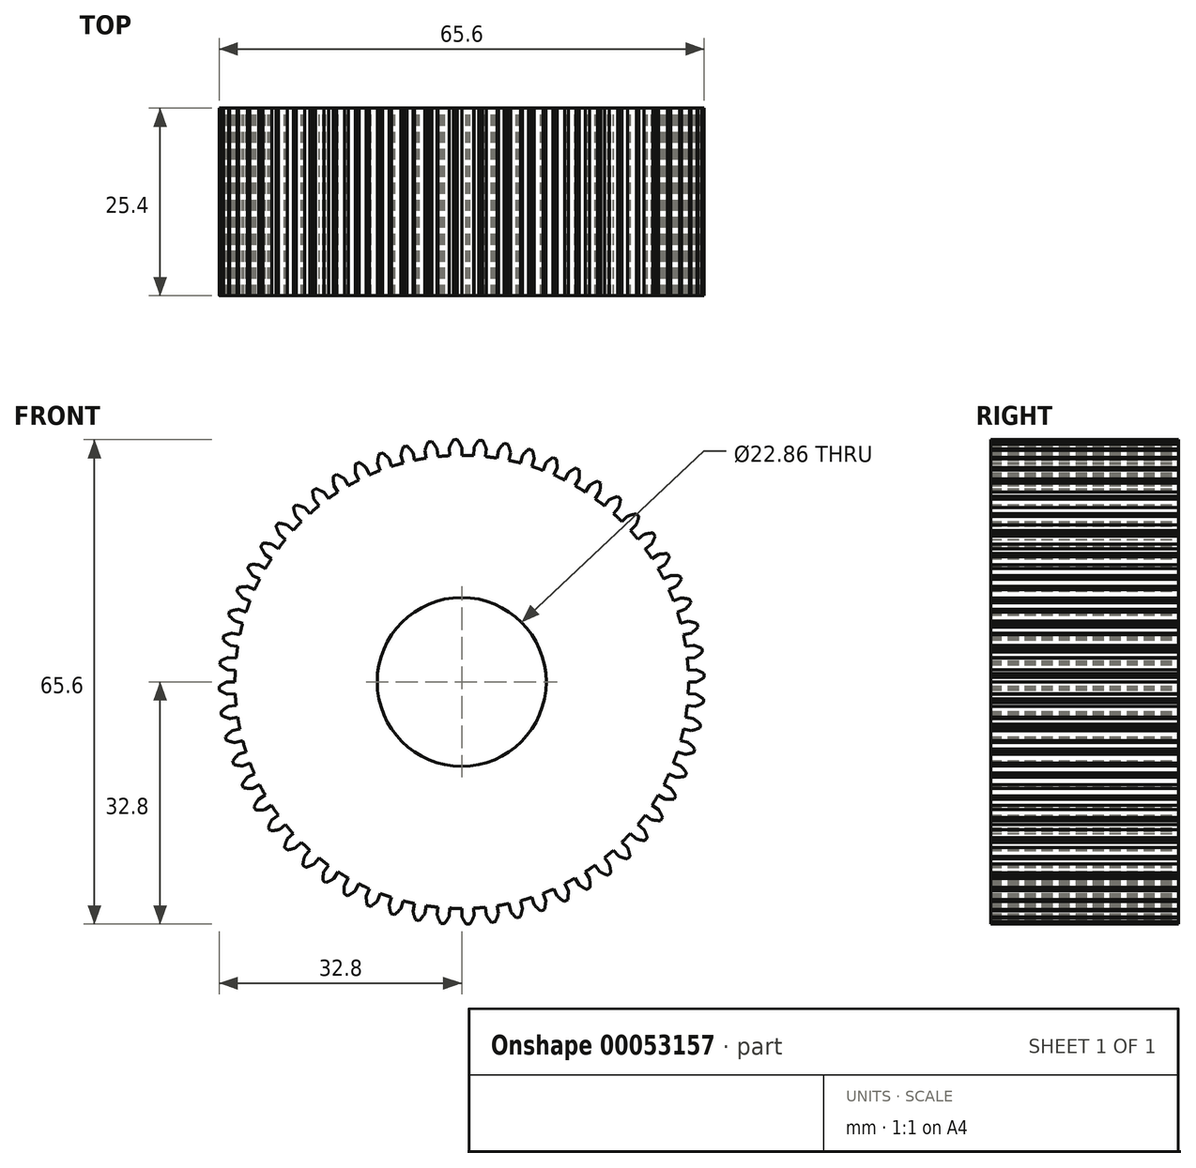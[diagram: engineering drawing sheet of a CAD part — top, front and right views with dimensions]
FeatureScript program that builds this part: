
annotation { "Feature Type Name" : "Feature", "Feature Type Description" : "" }
export const myFeature = defineFeature(function(context is Context, id is Id, definition is map)
    precondition{}
    {
        {
            var Q0;
            Q0=qCreatedBy(makeId("Front.planeOp"),FACE);
            var sketch = newSketch(context, id + "F0", { "sketchPlane" : qUnion([Q0])});
            skArc(sketch, "E0", {"start": v(-7.94, 29.64) * mm, "mid": v(-8.71, 29.42) * mm, "end": v(-9.48, 29.18) * mm});
            skArc(sketch, "E1.trimOffspring", {"start": v(0, 31.75) * mm, "mid": v(-0.28, 32.29) * mm, "end": v(-0.6, 32.8) * mm});
            skLineSegment(sketch, "E2", {"start": v(0, 31.75) * mm, "end": v(0, 30.68) * mm});
            skLineSegment(sketch, "E3", {"start": v(-0.6, 32.8) * mm, "end": v(-0.86, 32.8) * mm});
            skLineSegment(sketch, "E4.MirrorCS", {"start": v(-1.12, 32.79) * mm, "end": v(-0.86, 32.8) * mm});
            skArc(sketch, "E5.MirrorCS", {"start": v(-1.66, 31.7) * mm, "mid": v(-1.4, 32.26) * mm, "end": v(-1.12, 32.79) * mm});
            skLineSegment(sketch, "E6.MirrorCS", {"start": v(-1.66, 31.7) * mm, "end": v(-1.6, 30.64) * mm});
            skLineSegment(sketch, "E7.1.0", {"start": v(-4.97, 31.36) * mm, "end": v(-4.8, 30.3) * mm});
            skArc(sketch, "E7.1.1", {"start": v(-4.97, 31.36) * mm, "mid": v(-4.77, 31.93) * mm, "end": v(-4.54, 32.49) * mm});
            skLineSegment(sketch, "E7.1.2", {"start": v(-4.54, 32.49) * mm, "end": v(-4.28, 32.52) * mm});
            skLineSegment(sketch, "E7.1.3", {"start": v(-4.03, 32.56) * mm, "end": v(-4.28, 32.52) * mm});
            skArc(sketch, "E7.1.4", {"start": v(-3.32, 31.58) * mm, "mid": v(-3.65, 32.08) * mm, "end": v(-4.03, 32.56) * mm});
            skLineSegment(sketch, "E7.1.5", {"start": v(-3.32, 31.58) * mm, "end": v(-3.2, 30.52) * mm});
            skLineSegment(sketch, "E7.2.0", {"start": v(-8.22, 30.67) * mm, "end": v(-7.94, 29.64) * mm});
            skArc(sketch, "E7.2.1", {"start": v(-8.22, 30.67) * mm, "mid": v(-8.08, 31.26) * mm, "end": v(-7.9, 31.84) * mm});
            skLineSegment(sketch, "E7.2.2", {"start": v(-7.9, 31.84) * mm, "end": v(-7.66, 31.9) * mm});
            skLineSegment(sketch, "E7.2.3", {"start": v(-7.4, 31.96) * mm, "end": v(-7.66, 31.9) * mm});
            skArc(sketch, "E7.2.4", {"start": v(-6.6, 31.06) * mm, "mid": v(-6.99, 31.52) * mm, "end": v(-7.4, 31.96) * mm});
            skLineSegment(sketch, "E7.2.5", {"start": v(-6.6, 31.06) * mm, "end": v(-6.38, 30.01) * mm});
            skLineSegment(sketch, "E7.3.0", {"start": v(-11.38, 29.64) * mm, "end": v(-11, 28.65) * mm});
            skArc(sketch, "E7.3.1", {"start": v(-11.38, 29.64) * mm, "mid": v(-11.3, 30.24) * mm, "end": v(-11.2, 30.84) * mm});
            skLineSegment(sketch, "E7.3.2", {"start": v(-11.2, 30.84) * mm, "end": v(-10.95, 30.92) * mm});
            skLineSegment(sketch, "E7.3.3", {"start": v(-10.7, 31) * mm, "end": v(-10.95, 30.92) * mm});
            skArc(sketch, "E7.3.4", {"start": v(-9.81, 30.2) * mm, "mid": v(-10.24, 30.62) * mm, "end": v(-10.7, 31) * mm});
            skLineSegment(sketch, "E7.3.5", {"start": v(-9.81, 30.2) * mm, "end": v(-9.48, 29.18) * mm});
            skLineSegment(sketch, "E7.4.0", {"start": v(-14.41, 28.29) * mm, "end": v(-13.93, 27.34) * mm});
            skArc(sketch, "E7.4.1", {"start": v(-14.41, 28.29) * mm, "mid": v(-14.4, 28.9) * mm, "end": v(-14.35, 29.5) * mm});
            skLineSegment(sketch, "E7.4.2", {"start": v(-14.35, 29.5) * mm, "end": v(-14.12, 29.6) * mm});
            skLineSegment(sketch, "E7.4.3", {"start": v(-13.9, 29.72) * mm, "end": v(-14.12, 29.6) * mm});
            skArc(sketch, "E7.4.4", {"start": v(-12.91, 29) * mm, "mid": v(-13.39, 29.38) * mm, "end": v(-13.9, 29.72) * mm});
            skLineSegment(sketch, "E7.4.5", {"start": v(-12.91, 29) * mm, "end": v(-12.48, 28.03) * mm});
            skLineSegment(sketch, "E7.5.0", {"start": v(-17.3, 26.63) * mm, "end": v(-16.71, 25.73) * mm});
            skArc(sketch, "E7.5.1", {"start": v(-17.3, 26.63) * mm, "mid": v(-17.35, 27.23) * mm, "end": v(-17.36, 27.84) * mm});
            skLineSegment(sketch, "E7.5.2", {"start": v(-17.36, 27.84) * mm, "end": v(-17.14, 27.97) * mm});
            skLineSegment(sketch, "E7.5.3", {"start": v(-16.92, 28.1) * mm, "end": v(-17.14, 27.97) * mm});
            skArc(sketch, "E7.5.4", {"start": v(-15.88, 27.5) * mm, "mid": v(-16.39, 27.82) * mm, "end": v(-16.92, 28.1) * mm});
            skLineSegment(sketch, "E7.5.5", {"start": v(-15.87, 27.5) * mm, "end": v(-15.34, 26.57) * mm});
            skLineSegment(sketch, "E7.6.0", {"start": v(-19.98, 24.67) * mm, "end": v(-19.3, 23.85) * mm});
            skArc(sketch, "E7.6.1", {"start": v(-19.98, 24.67) * mm, "mid": v(-20.1, 25.27) * mm, "end": v(-20.17, 25.87) * mm});
            skLineSegment(sketch, "E7.6.2", {"start": v(-20.17, 25.87) * mm, "end": v(-19.97, 26.03) * mm});
            skLineSegment(sketch, "E7.6.3", {"start": v(-19.77, 26.18) * mm, "end": v(-19.97, 26.03) * mm});
            skArc(sketch, "E7.6.4", {"start": v(-18.66, 25.69) * mm, "mid": v(-19.2, 25.95) * mm, "end": v(-19.77, 26.18) * mm});
            skLineSegment(sketch, "E7.6.5", {"start": v(-18.66, 25.69) * mm, "end": v(-18.04, 24.82) * mm});
            skLineSegment(sketch, "E7.7.0", {"start": v(-22.45, 22.45) * mm, "end": v(-21.7, 21.7) * mm});
            skArc(sketch, "E7.7.1", {"start": v(-22.45, 22.45) * mm, "mid": v(-22.63, 23.03) * mm, "end": v(-22.77, 23.62) * mm});
            skLineSegment(sketch, "E7.7.2", {"start": v(-22.77, 23.62) * mm, "end": v(-22.58, 23.8) * mm});
            skLineSegment(sketch, "E7.7.3", {"start": v(-22.4, 23.97) * mm, "end": v(-22.58, 23.8) * mm});
            skArc(sketch, "E7.7.4", {"start": v(-21.24, 23.6) * mm, "mid": v(-21.81, 23.8) * mm, "end": v(-22.4, 23.97) * mm});
            skLineSegment(sketch, "E7.7.5", {"start": v(-21.24, 23.6) * mm, "end": v(-20.53, 22.8) * mm});
            skLineSegment(sketch, "E7.8.0", {"start": v(-24.67, 19.98) * mm, "end": v(-23.85, 19.3) * mm});
            skArc(sketch, "E7.8.1", {"start": v(-24.67, 19.98) * mm, "mid": v(-24.91, 20.54) * mm, "end": v(-25.11, 21.1) * mm});
            skLineSegment(sketch, "E7.8.2", {"start": v(-25.11, 21.1) * mm, "end": v(-24.95, 21.3) * mm});
            skLineSegment(sketch, "E7.8.3", {"start": v(-24.78, 21.5) * mm, "end": v(-24.95, 21.3) * mm});
            skArc(sketch, "E7.8.4", {"start": v(-23.6, 21.24) * mm, "mid": v(-24.18, 21.4) * mm, "end": v(-24.78, 21.5) * mm});
            skLineSegment(sketch, "E7.8.5", {"start": v(-23.6, 21.24) * mm, "end": v(-22.8, 20.53) * mm});
            skLineSegment(sketch, "E7.9.0", {"start": v(-26.63, 17.3) * mm, "end": v(-25.73, 16.71) * mm});
            skArc(sketch, "E7.9.1", {"start": v(-26.63, 17.3) * mm, "mid": v(-26.92, 17.82) * mm, "end": v(-27.18, 18.37) * mm});
            skLineSegment(sketch, "E7.9.2", {"start": v(-27.18, 18.37) * mm, "end": v(-27.04, 18.58) * mm});
            skLineSegment(sketch, "E7.9.3", {"start": v(-26.89, 18.8) * mm, "end": v(-27.04, 18.58) * mm});
            skArc(sketch, "E7.9.4", {"start": v(-25.69, 18.66) * mm, "mid": v(-26.28, 18.75) * mm, "end": v(-26.89, 18.8) * mm});
            skLineSegment(sketch, "E7.9.5", {"start": v(-25.69, 18.66) * mm, "end": v(-24.82, 18.04) * mm});
            skLineSegment(sketch, "E7.10.0", {"start": v(-28.29, 14.41) * mm, "end": v(-27.34, 13.93) * mm});
            skArc(sketch, "E7.10.1", {"start": v(-28.29, 14.41) * mm, "mid": v(-28.64, 14.9) * mm, "end": v(-28.95, 15.43) * mm});
            skLineSegment(sketch, "E7.10.2", {"start": v(-28.95, 15.43) * mm, "end": v(-28.83, 15.65) * mm});
            skLineSegment(sketch, "E7.10.3", {"start": v(-28.7, 15.88) * mm, "end": v(-28.83, 15.65) * mm});
            skArc(sketch, "E7.10.4", {"start": v(-27.5, 15.88) * mm, "mid": v(-28.1, 15.9) * mm, "end": v(-28.7, 15.88) * mm});
            skLineSegment(sketch, "E7.10.5", {"start": v(-27.5, 15.88) * mm, "end": v(-26.57, 15.34) * mm});
            skLineSegment(sketch, "E7.11.0", {"start": v(-29.64, 11.38) * mm, "end": v(-28.65, 11) * mm});
            skArc(sketch, "E7.11.1", {"start": v(-29.64, 11.38) * mm, "mid": v(-30.04, 11.83) * mm, "end": v(-30.4, 12.32) * mm});
            skLineSegment(sketch, "E7.11.2", {"start": v(-30.4, 12.32) * mm, "end": v(-30.3, 12.55) * mm});
            skLineSegment(sketch, "E7.11.3", {"start": v(-30.2, 12.8) * mm, "end": v(-30.3, 12.55) * mm});
            skArc(sketch, "E7.11.4", {"start": v(-29, 12.91) * mm, "mid": v(-29.6, 12.88) * mm, "end": v(-30.2, 12.8) * mm});
            skLineSegment(sketch, "E7.11.5", {"start": v(-29, 12.91) * mm, "end": v(-28.03, 12.48) * mm});
            skLineSegment(sketch, "E7.12.0", {"start": v(-30.67, 8.22) * mm, "end": v(-29.64, 7.94) * mm});
            skArc(sketch, "E7.12.1", {"start": v(-30.67, 8.22) * mm, "mid": v(-31.11, 8.63) * mm, "end": v(-31.53, 9.07) * mm});
            skLineSegment(sketch, "E7.12.2", {"start": v(-31.53, 9.07) * mm, "end": v(-31.45, 9.32) * mm});
            skLineSegment(sketch, "E7.12.3", {"start": v(-31.38, 9.56) * mm, "end": v(-31.45, 9.32) * mm});
            skArc(sketch, "E7.12.4", {"start": v(-30.2, 9.81) * mm, "mid": v(-30.8, 9.7) * mm, "end": v(-31.38, 9.56) * mm});
            skLineSegment(sketch, "E7.12.5", {"start": v(-30.2, 9.81) * mm, "end": v(-29.18, 9.48) * mm});
            skLineSegment(sketch, "E7.13.0", {"start": v(-31.36, 4.97) * mm, "end": v(-30.3, 4.8) * mm});
            skArc(sketch, "E7.13.1", {"start": v(-31.36, 4.97) * mm, "mid": v(-31.84, 5.33) * mm, "end": v(-32.3, 5.73) * mm});
            skLineSegment(sketch, "E7.13.2", {"start": v(-32.3, 5.73) * mm, "end": v(-32.26, 5.98) * mm});
            skLineSegment(sketch, "E7.13.3", {"start": v(-32.2, 6.23) * mm, "end": v(-32.26, 5.98) * mm});
            skArc(sketch, "E7.13.4", {"start": v(-31.06, 6.6) * mm, "mid": v(-31.64, 6.44) * mm, "end": v(-32.2, 6.23) * mm});
            skLineSegment(sketch, "E7.13.5", {"start": v(-31.06, 6.6) * mm, "end": v(-30.01, 6.38) * mm});
            skLineSegment(sketch, "E7.14.0", {"start": v(-31.7, 1.66) * mm, "end": v(-30.64, 1.6) * mm});
            skArc(sketch, "E7.14.1", {"start": v(-31.7, 1.66) * mm, "mid": v(-32.23, 1.97) * mm, "end": v(-32.72, 2.32) * mm});
            skLineSegment(sketch, "E7.14.2", {"start": v(-32.72, 2.32) * mm, "end": v(-32.7, 2.57) * mm});
            skLineSegment(sketch, "E7.14.3", {"start": v(-32.68, 2.83) * mm, "end": v(-32.7, 2.57) * mm});
            skArc(sketch, "E7.14.4", {"start": v(-31.58, 3.32) * mm, "mid": v(-32.14, 3.1) * mm, "end": v(-32.68, 2.83) * mm});
            skLineSegment(sketch, "E7.14.5", {"start": v(-31.58, 3.32) * mm, "end": v(-30.52, 3.2) * mm});
            skLineSegment(sketch, "E7.15.0", {"start": v(-31.7, -1.66) * mm, "end": v(-30.64, -1.6) * mm});
            skArc(sketch, "E7.15.1", {"start": v(-31.7, -1.66) * mm, "mid": v(-32.26, -1.4) * mm, "end": v(-32.79, -1.12) * mm});
            skLineSegment(sketch, "E7.15.2", {"start": v(-32.79, -1.12) * mm, "end": v(-32.8, -0.86) * mm});
            skLineSegment(sketch, "E7.15.3", {"start": v(-32.8, -0.6) * mm, "end": v(-32.8, -0.86) * mm});
            skArc(sketch, "E7.15.4", {"start": v(-31.75, 0) * mm, "mid": v(-32.29, -0.28) * mm, "end": v(-32.8, -0.6) * mm});
            skLineSegment(sketch, "E7.15.5", {"start": v(-31.75, 0) * mm, "end": v(-30.68, 0) * mm});
            skLineSegment(sketch, "E7.16.0", {"start": v(-31.36, -4.97) * mm, "end": v(-30.3, -4.8) * mm});
            skArc(sketch, "E7.16.1", {"start": v(-31.36, -4.97) * mm, "mid": v(-31.93, -4.77) * mm, "end": v(-32.49, -4.54) * mm});
            skLineSegment(sketch, "E7.16.2", {"start": v(-32.49, -4.54) * mm, "end": v(-32.52, -4.28) * mm});
            skLineSegment(sketch, "E7.16.3", {"start": v(-32.56, -4.03) * mm, "end": v(-32.52, -4.28) * mm});
            skArc(sketch, "E7.16.4", {"start": v(-31.58, -3.32) * mm, "mid": v(-32.08, -3.65) * mm, "end": v(-32.56, -4.03) * mm});
            skLineSegment(sketch, "E7.16.5", {"start": v(-31.58, -3.32) * mm, "end": v(-30.52, -3.2) * mm});
            skLineSegment(sketch, "E7.17.0", {"start": v(-30.67, -8.22) * mm, "end": v(-29.64, -7.94) * mm});
            skArc(sketch, "E7.17.1", {"start": v(-30.67, -8.22) * mm, "mid": v(-31.26, -8.08) * mm, "end": v(-31.84, -7.9) * mm});
            skLineSegment(sketch, "E7.17.2", {"start": v(-31.84, -7.9) * mm, "end": v(-31.9, -7.66) * mm});
            skLineSegment(sketch, "E7.17.3", {"start": v(-31.96, -7.4) * mm, "end": v(-31.9, -7.66) * mm});
            skArc(sketch, "E7.17.4", {"start": v(-31.06, -6.6) * mm, "mid": v(-31.52, -6.99) * mm, "end": v(-31.96, -7.4) * mm});
            skLineSegment(sketch, "E7.17.5", {"start": v(-31.06, -6.6) * mm, "end": v(-30.01, -6.38) * mm});
            skLineSegment(sketch, "E7.18.0", {"start": v(-29.64, -11.38) * mm, "end": v(-28.65, -11) * mm});
            skArc(sketch, "E7.18.1", {"start": v(-29.64, -11.38) * mm, "mid": v(-30.24, -11.3) * mm, "end": v(-30.84, -11.2) * mm});
            skLineSegment(sketch, "E7.18.2", {"start": v(-30.84, -11.2) * mm, "end": v(-30.92, -10.95) * mm});
            skLineSegment(sketch, "E7.18.3", {"start": v(-31, -10.7) * mm, "end": v(-30.92, -10.95) * mm});
            skArc(sketch, "E7.18.4", {"start": v(-30.2, -9.81) * mm, "mid": v(-30.62, -10.24) * mm, "end": v(-31, -10.7) * mm});
            skLineSegment(sketch, "E7.18.5", {"start": v(-30.2, -9.81) * mm, "end": v(-29.18, -9.48) * mm});
            skLineSegment(sketch, "E7.19.0", {"start": v(-28.29, -14.41) * mm, "end": v(-27.34, -13.93) * mm});
            skArc(sketch, "E7.19.1", {"start": v(-28.29, -14.41) * mm, "mid": v(-28.9, -14.4) * mm, "end": v(-29.5, -14.35) * mm});
            skLineSegment(sketch, "E7.19.2", {"start": v(-29.5, -14.35) * mm, "end": v(-29.6, -14.12) * mm});
            skLineSegment(sketch, "E7.19.3", {"start": v(-29.72, -13.9) * mm, "end": v(-29.6, -14.12) * mm});
            skArc(sketch, "E7.19.4", {"start": v(-29, -12.91) * mm, "mid": v(-29.38, -13.39) * mm, "end": v(-29.72, -13.9) * mm});
            skLineSegment(sketch, "E7.19.5", {"start": v(-29, -12.91) * mm, "end": v(-28.03, -12.48) * mm});
            skLineSegment(sketch, "E7.20.0", {"start": v(-26.63, -17.3) * mm, "end": v(-25.73, -16.71) * mm});
            skArc(sketch, "E7.20.1", {"start": v(-26.63, -17.3) * mm, "mid": v(-27.23, -17.35) * mm, "end": v(-27.84, -17.36) * mm});
            skLineSegment(sketch, "E7.20.2", {"start": v(-27.84, -17.36) * mm, "end": v(-27.97, -17.14) * mm});
            skLineSegment(sketch, "E7.20.3", {"start": v(-28.1, -16.92) * mm, "end": v(-27.97, -17.14) * mm});
            skArc(sketch, "E7.20.4", {"start": v(-27.5, -15.87) * mm, "mid": v(-27.82, -16.39) * mm, "end": v(-28.1, -16.92) * mm});
            skLineSegment(sketch, "E7.20.5", {"start": v(-27.5, -15.87) * mm, "end": v(-26.57, -15.34) * mm});
            skLineSegment(sketch, "E7.21.0", {"start": v(-24.67, -19.98) * mm, "end": v(-23.85, -19.3) * mm});
            skArc(sketch, "E7.21.1", {"start": v(-24.67, -19.98) * mm, "mid": v(-25.27, -20.1) * mm, "end": v(-25.87, -20.17) * mm});
            skLineSegment(sketch, "E7.21.2", {"start": v(-25.87, -20.17) * mm, "end": v(-26.03, -19.97) * mm});
            skLineSegment(sketch, "E7.21.3", {"start": v(-26.18, -19.77) * mm, "end": v(-26.03, -19.97) * mm});
            skArc(sketch, "E7.21.4", {"start": v(-25.69, -18.66) * mm, "mid": v(-25.95, -19.2) * mm, "end": v(-26.18, -19.77) * mm});
            skLineSegment(sketch, "E7.21.5", {"start": v(-25.69, -18.66) * mm, "end": v(-24.82, -18.04) * mm});
            skLineSegment(sketch, "E7.22.0", {"start": v(-22.45, -22.45) * mm, "end": v(-21.7, -21.7) * mm});
            skArc(sketch, "E7.22.1", {"start": v(-22.45, -22.45) * mm, "mid": v(-23.03, -22.63) * mm, "end": v(-23.62, -22.77) * mm});
            skLineSegment(sketch, "E7.22.2", {"start": v(-23.62, -22.77) * mm, "end": v(-23.8, -22.58) * mm});
            skLineSegment(sketch, "E7.22.3", {"start": v(-23.97, -22.4) * mm, "end": v(-23.8, -22.58) * mm});
            skArc(sketch, "E7.22.4", {"start": v(-23.6, -21.24) * mm, "mid": v(-23.8, -21.81) * mm, "end": v(-23.97, -22.4) * mm});
            skLineSegment(sketch, "E7.22.5", {"start": v(-23.6, -21.24) * mm, "end": v(-22.8, -20.53) * mm});
            skLineSegment(sketch, "E7.23.0", {"start": v(-19.98, -24.67) * mm, "end": v(-19.3, -23.85) * mm});
            skArc(sketch, "E7.23.1", {"start": v(-19.98, -24.67) * mm, "mid": v(-20.54, -24.91) * mm, "end": v(-21.1, -25.11) * mm});
            skLineSegment(sketch, "E7.23.2", {"start": v(-21.1, -25.11) * mm, "end": v(-21.3, -24.95) * mm});
            skLineSegment(sketch, "E7.23.3", {"start": v(-21.5, -24.78) * mm, "end": v(-21.3, -24.95) * mm});
            skArc(sketch, "E7.23.4", {"start": v(-21.24, -23.6) * mm, "mid": v(-21.4, -24.18) * mm, "end": v(-21.5, -24.78) * mm});
            skLineSegment(sketch, "E7.23.5", {"start": v(-21.24, -23.6) * mm, "end": v(-20.53, -22.8) * mm});
            skLineSegment(sketch, "E7.24.0", {"start": v(-17.3, -26.63) * mm, "end": v(-16.71, -25.73) * mm});
            skArc(sketch, "E7.24.1", {"start": v(-17.3, -26.63) * mm, "mid": v(-17.82, -26.92) * mm, "end": v(-18.37, -27.18) * mm});
            skLineSegment(sketch, "E7.24.2", {"start": v(-18.37, -27.18) * mm, "end": v(-18.58, -27.04) * mm});
            skLineSegment(sketch, "E7.24.3", {"start": v(-18.8, -26.89) * mm, "end": v(-18.58, -27.04) * mm});
            skArc(sketch, "E7.24.4", {"start": v(-18.66, -25.69) * mm, "mid": v(-18.75, -26.28) * mm, "end": v(-18.8, -26.89) * mm});
            skLineSegment(sketch, "E7.24.5", {"start": v(-18.66, -25.69) * mm, "end": v(-18.04, -24.82) * mm});
            skLineSegment(sketch, "E7.25.0", {"start": v(-14.41, -28.29) * mm, "end": v(-13.93, -27.34) * mm});
            skArc(sketch, "E7.25.1", {"start": v(-14.41, -28.29) * mm, "mid": v(-14.9, -28.64) * mm, "end": v(-15.43, -28.95) * mm});
            skLineSegment(sketch, "E7.25.2", {"start": v(-15.43, -28.95) * mm, "end": v(-15.65, -28.83) * mm});
            skLineSegment(sketch, "E7.25.3", {"start": v(-15.88, -28.7) * mm, "end": v(-15.65, -28.83) * mm});
            skArc(sketch, "E7.25.4", {"start": v(-15.87, -27.5) * mm, "mid": v(-15.9, -28.1) * mm, "end": v(-15.88, -28.7) * mm});
            skLineSegment(sketch, "E7.25.5", {"start": v(-15.87, -27.5) * mm, "end": v(-15.34, -26.57) * mm});
            skLineSegment(sketch, "E7.26.0", {"start": v(-11.38, -29.64) * mm, "end": v(-11, -28.65) * mm});
            skArc(sketch, "E7.26.1", {"start": v(-11.38, -29.64) * mm, "mid": v(-11.83, -30.04) * mm, "end": v(-12.32, -30.4) * mm});
            skLineSegment(sketch, "E7.26.2", {"start": v(-12.32, -30.4) * mm, "end": v(-12.55, -30.3) * mm});
            skLineSegment(sketch, "E7.26.3", {"start": v(-12.8, -30.2) * mm, "end": v(-12.55, -30.3) * mm});
            skArc(sketch, "E7.26.4", {"start": v(-12.91, -29) * mm, "mid": v(-12.88, -29.6) * mm, "end": v(-12.8, -30.2) * mm});
            skLineSegment(sketch, "E7.26.5", {"start": v(-12.91, -29) * mm, "end": v(-12.48, -28.03) * mm});
            skLineSegment(sketch, "E7.27.0", {"start": v(-8.22, -30.67) * mm, "end": v(-7.94, -29.64) * mm});
            skArc(sketch, "E7.27.1", {"start": v(-8.22, -30.67) * mm, "mid": v(-8.63, -31.11) * mm, "end": v(-9.07, -31.53) * mm});
            skLineSegment(sketch, "E7.27.2", {"start": v(-9.07, -31.53) * mm, "end": v(-9.32, -31.45) * mm});
            skLineSegment(sketch, "E7.27.3", {"start": v(-9.56, -31.38) * mm, "end": v(-9.32, -31.45) * mm});
            skArc(sketch, "E7.27.4", {"start": v(-9.81, -30.2) * mm, "mid": v(-9.7, -30.8) * mm, "end": v(-9.56, -31.38) * mm});
            skLineSegment(sketch, "E7.27.5", {"start": v(-9.81, -30.2) * mm, "end": v(-9.48, -29.18) * mm});
            skLineSegment(sketch, "E7.28.0", {"start": v(-4.97, -31.36) * mm, "end": v(-4.8, -30.3) * mm});
            skArc(sketch, "E7.28.1", {"start": v(-4.97, -31.36) * mm, "mid": v(-5.33, -31.84) * mm, "end": v(-5.73, -32.3) * mm});
            skLineSegment(sketch, "E7.28.2", {"start": v(-5.73, -32.3) * mm, "end": v(-5.98, -32.26) * mm});
            skLineSegment(sketch, "E7.28.3", {"start": v(-6.23, -32.2) * mm, "end": v(-5.98, -32.26) * mm});
            skArc(sketch, "E7.28.4", {"start": v(-6.6, -31.06) * mm, "mid": v(-6.44, -31.64) * mm, "end": v(-6.23, -32.2) * mm});
            skLineSegment(sketch, "E7.28.5", {"start": v(-6.6, -31.06) * mm, "end": v(-6.38, -30.01) * mm});
            skLineSegment(sketch, "E7.29.0", {"start": v(-1.66, -31.7) * mm, "end": v(-1.6, -30.64) * mm});
            skArc(sketch, "E7.29.1", {"start": v(-1.66, -31.7) * mm, "mid": v(-1.97, -32.23) * mm, "end": v(-2.32, -32.72) * mm});
            skLineSegment(sketch, "E7.29.2", {"start": v(-2.32, -32.72) * mm, "end": v(-2.57, -32.7) * mm});
            skLineSegment(sketch, "E7.29.3", {"start": v(-2.83, -32.68) * mm, "end": v(-2.57, -32.7) * mm});
            skArc(sketch, "E7.29.4", {"start": v(-3.32, -31.58) * mm, "mid": v(-3.1, -32.14) * mm, "end": v(-2.83, -32.68) * mm});
            skLineSegment(sketch, "E7.29.5", {"start": v(-3.32, -31.58) * mm, "end": v(-3.2, -30.52) * mm});
            skLineSegment(sketch, "E7.30.0", {"start": v(1.66, -31.7) * mm, "end": v(1.6, -30.64) * mm});
            skArc(sketch, "E7.30.1", {"start": v(1.66, -31.7) * mm, "mid": v(1.4, -32.26) * mm, "end": v(1.12, -32.79) * mm});
            skLineSegment(sketch, "E7.30.2", {"start": v(1.12, -32.79) * mm, "end": v(0.86, -32.8) * mm});
            skLineSegment(sketch, "E7.30.3", {"start": v(0.6, -32.8) * mm, "end": v(0.86, -32.8) * mm});
            skArc(sketch, "E7.30.4", {"start": v(0, -31.75) * mm, "mid": v(0.28, -32.29) * mm, "end": v(0.6, -32.8) * mm});
            skLineSegment(sketch, "E7.30.5", {"start": v(0, -31.75) * mm, "end": v(0, -30.68) * mm});
            skLineSegment(sketch, "E7.31.0", {"start": v(4.97, -31.36) * mm, "end": v(4.8, -30.3) * mm});
            skArc(sketch, "E7.31.1", {"start": v(4.97, -31.36) * mm, "mid": v(4.77, -31.93) * mm, "end": v(4.54, -32.49) * mm});
            skLineSegment(sketch, "E7.31.2", {"start": v(4.54, -32.49) * mm, "end": v(4.28, -32.52) * mm});
            skLineSegment(sketch, "E7.31.3", {"start": v(4.03, -32.56) * mm, "end": v(4.28, -32.52) * mm});
            skArc(sketch, "E7.31.4", {"start": v(3.32, -31.58) * mm, "mid": v(3.65, -32.08) * mm, "end": v(4.03, -32.56) * mm});
            skLineSegment(sketch, "E7.31.5", {"start": v(3.32, -31.58) * mm, "end": v(3.2, -30.52) * mm});
            skLineSegment(sketch, "E7.32.0", {"start": v(8.22, -30.67) * mm, "end": v(7.94, -29.64) * mm});
            skArc(sketch, "E7.32.1", {"start": v(8.22, -30.67) * mm, "mid": v(8.08, -31.26) * mm, "end": v(7.9, -31.84) * mm});
            skLineSegment(sketch, "E7.32.2", {"start": v(7.9, -31.84) * mm, "end": v(7.66, -31.9) * mm});
            skLineSegment(sketch, "E7.32.3", {"start": v(7.4, -31.96) * mm, "end": v(7.66, -31.9) * mm});
            skArc(sketch, "E7.32.4", {"start": v(6.6, -31.06) * mm, "mid": v(6.99, -31.52) * mm, "end": v(7.4, -31.96) * mm});
            skLineSegment(sketch, "E7.32.5", {"start": v(6.6, -31.06) * mm, "end": v(6.38, -30.01) * mm});
            skLineSegment(sketch, "E7.33.0", {"start": v(11.38, -29.64) * mm, "end": v(11, -28.65) * mm});
            skArc(sketch, "E7.33.1", {"start": v(11.38, -29.64) * mm, "mid": v(11.3, -30.24) * mm, "end": v(11.2, -30.84) * mm});
            skLineSegment(sketch, "E7.33.2", {"start": v(11.2, -30.84) * mm, "end": v(10.95, -30.92) * mm});
            skLineSegment(sketch, "E7.33.3", {"start": v(10.7, -31) * mm, "end": v(10.95, -30.92) * mm});
            skArc(sketch, "E7.33.4", {"start": v(9.81, -30.2) * mm, "mid": v(10.24, -30.62) * mm, "end": v(10.7, -31) * mm});
            skLineSegment(sketch, "E7.33.5", {"start": v(9.81, -30.2) * mm, "end": v(9.48, -29.18) * mm});
            skLineSegment(sketch, "E7.34.0", {"start": v(14.41, -28.29) * mm, "end": v(13.93, -27.34) * mm});
            skArc(sketch, "E7.34.1", {"start": v(14.41, -28.29) * mm, "mid": v(14.4, -28.9) * mm, "end": v(14.35, -29.5) * mm});
            skLineSegment(sketch, "E7.34.2", {"start": v(14.35, -29.5) * mm, "end": v(14.12, -29.6) * mm});
            skLineSegment(sketch, "E7.34.3", {"start": v(13.9, -29.72) * mm, "end": v(14.12, -29.6) * mm});
            skArc(sketch, "E7.34.4", {"start": v(12.91, -29) * mm, "mid": v(13.39, -29.38) * mm, "end": v(13.9, -29.72) * mm});
            skLineSegment(sketch, "E7.34.5", {"start": v(12.91, -29) * mm, "end": v(12.48, -28.03) * mm});
            skLineSegment(sketch, "E7.35.0", {"start": v(17.3, -26.63) * mm, "end": v(16.71, -25.73) * mm});
            skArc(sketch, "E7.35.1", {"start": v(17.3, -26.63) * mm, "mid": v(17.35, -27.23) * mm, "end": v(17.36, -27.84) * mm});
            skLineSegment(sketch, "E7.35.2", {"start": v(17.36, -27.84) * mm, "end": v(17.14, -27.97) * mm});
            skLineSegment(sketch, "E7.35.3", {"start": v(16.92, -28.1) * mm, "end": v(17.14, -27.97) * mm});
            skArc(sketch, "E7.35.4", {"start": v(15.87, -27.5) * mm, "mid": v(16.39, -27.82) * mm, "end": v(16.92, -28.1) * mm});
            skLineSegment(sketch, "E7.35.5", {"start": v(15.87, -27.5) * mm, "end": v(15.34, -26.57) * mm});
            skLineSegment(sketch, "E7.36.0", {"start": v(19.98, -24.67) * mm, "end": v(19.3, -23.85) * mm});
            skArc(sketch, "E7.36.1", {"start": v(19.98, -24.67) * mm, "mid": v(20.1, -25.27) * mm, "end": v(20.17, -25.87) * mm});
            skLineSegment(sketch, "E7.36.2", {"start": v(20.17, -25.87) * mm, "end": v(19.97, -26.03) * mm});
            skLineSegment(sketch, "E7.36.3", {"start": v(19.77, -26.18) * mm, "end": v(19.97, -26.03) * mm});
            skArc(sketch, "E7.36.4", {"start": v(18.66, -25.69) * mm, "mid": v(19.2, -25.95) * mm, "end": v(19.77, -26.18) * mm});
            skLineSegment(sketch, "E7.36.5", {"start": v(18.66, -25.69) * mm, "end": v(18.04, -24.82) * mm});
            skLineSegment(sketch, "E7.37.0", {"start": v(22.45, -22.45) * mm, "end": v(21.7, -21.7) * mm});
            skArc(sketch, "E7.37.1", {"start": v(22.45, -22.45) * mm, "mid": v(22.63, -23.03) * mm, "end": v(22.77, -23.62) * mm});
            skLineSegment(sketch, "E7.37.2", {"start": v(22.77, -23.62) * mm, "end": v(22.58, -23.8) * mm});
            skLineSegment(sketch, "E7.37.3", {"start": v(22.4, -23.97) * mm, "end": v(22.58, -23.8) * mm});
            skArc(sketch, "E7.37.4", {"start": v(21.24, -23.6) * mm, "mid": v(21.81, -23.8) * mm, "end": v(22.4, -23.97) * mm});
            skLineSegment(sketch, "E7.37.5", {"start": v(21.24, -23.6) * mm, "end": v(20.53, -22.8) * mm});
            skLineSegment(sketch, "E7.38.0", {"start": v(24.67, -19.98) * mm, "end": v(23.85, -19.3) * mm});
            skArc(sketch, "E7.38.1", {"start": v(24.67, -19.98) * mm, "mid": v(24.91, -20.54) * mm, "end": v(25.11, -21.1) * mm});
            skLineSegment(sketch, "E7.38.2", {"start": v(25.11, -21.1) * mm, "end": v(24.95, -21.3) * mm});
            skLineSegment(sketch, "E7.38.3", {"start": v(24.78, -21.5) * mm, "end": v(24.95, -21.3) * mm});
            skArc(sketch, "E7.38.4", {"start": v(23.6, -21.24) * mm, "mid": v(24.18, -21.4) * mm, "end": v(24.78, -21.5) * mm});
            skLineSegment(sketch, "E7.38.5", {"start": v(23.6, -21.24) * mm, "end": v(22.8, -20.53) * mm});
            skLineSegment(sketch, "E7.39.0", {"start": v(26.63, -17.3) * mm, "end": v(25.73, -16.71) * mm});
            skArc(sketch, "E7.39.1", {"start": v(26.63, -17.3) * mm, "mid": v(26.92, -17.82) * mm, "end": v(27.18, -18.37) * mm});
            skLineSegment(sketch, "E7.39.2", {"start": v(27.18, -18.37) * mm, "end": v(27.04, -18.58) * mm});
            skLineSegment(sketch, "E7.39.3", {"start": v(26.89, -18.8) * mm, "end": v(27.04, -18.58) * mm});
            skArc(sketch, "E7.39.4", {"start": v(25.69, -18.66) * mm, "mid": v(26.28, -18.75) * mm, "end": v(26.89, -18.8) * mm});
            skLineSegment(sketch, "E7.39.5", {"start": v(25.69, -18.66) * mm, "end": v(24.82, -18.04) * mm});
            skLineSegment(sketch, "E7.40.0", {"start": v(28.29, -14.41) * mm, "end": v(27.34, -13.93) * mm});
            skArc(sketch, "E7.40.1", {"start": v(28.29, -14.41) * mm, "mid": v(28.64, -14.9) * mm, "end": v(28.95, -15.43) * mm});
            skLineSegment(sketch, "E7.40.2", {"start": v(28.95, -15.43) * mm, "end": v(28.83, -15.65) * mm});
            skLineSegment(sketch, "E7.40.3", {"start": v(28.7, -15.88) * mm, "end": v(28.83, -15.65) * mm});
            skArc(sketch, "E7.40.4", {"start": v(27.5, -15.88) * mm, "mid": v(28.1, -15.9) * mm, "end": v(28.7, -15.88) * mm});
            skLineSegment(sketch, "E7.40.5", {"start": v(27.5, -15.88) * mm, "end": v(26.57, -15.34) * mm});
            skLineSegment(sketch, "E7.41.0", {"start": v(29.64, -11.38) * mm, "end": v(28.65, -11) * mm});
            skArc(sketch, "E7.41.1", {"start": v(29.64, -11.38) * mm, "mid": v(30.04, -11.83) * mm, "end": v(30.4, -12.32) * mm});
            skLineSegment(sketch, "E7.41.2", {"start": v(30.4, -12.32) * mm, "end": v(30.3, -12.55) * mm});
            skLineSegment(sketch, "E7.41.3", {"start": v(30.2, -12.8) * mm, "end": v(30.3, -12.55) * mm});
            skArc(sketch, "E7.41.4", {"start": v(29, -12.91) * mm, "mid": v(29.6, -12.88) * mm, "end": v(30.2, -12.8) * mm});
            skLineSegment(sketch, "E7.41.5", {"start": v(29, -12.91) * mm, "end": v(28.03, -12.48) * mm});
            skLineSegment(sketch, "E7.42.0", {"start": v(30.67, -8.22) * mm, "end": v(29.64, -7.94) * mm});
            skArc(sketch, "E7.42.1", {"start": v(30.67, -8.22) * mm, "mid": v(31.11, -8.63) * mm, "end": v(31.53, -9.07) * mm});
            skLineSegment(sketch, "E7.42.2", {"start": v(31.53, -9.07) * mm, "end": v(31.45, -9.32) * mm});
            skLineSegment(sketch, "E7.42.3", {"start": v(31.38, -9.56) * mm, "end": v(31.45, -9.32) * mm});
            skArc(sketch, "E7.42.4", {"start": v(30.2, -9.81) * mm, "mid": v(30.8, -9.7) * mm, "end": v(31.38, -9.56) * mm});
            skLineSegment(sketch, "E7.42.5", {"start": v(30.2, -9.81) * mm, "end": v(29.18, -9.48) * mm});
            skLineSegment(sketch, "E7.43.0", {"start": v(31.36, -4.97) * mm, "end": v(30.3, -4.8) * mm});
            skArc(sketch, "E7.43.1", {"start": v(31.36, -4.97) * mm, "mid": v(31.84, -5.33) * mm, "end": v(32.3, -5.73) * mm});
            skLineSegment(sketch, "E7.43.2", {"start": v(32.3, -5.73) * mm, "end": v(32.26, -5.98) * mm});
            skLineSegment(sketch, "E7.43.3", {"start": v(32.2, -6.23) * mm, "end": v(32.26, -5.98) * mm});
            skArc(sketch, "E7.43.4", {"start": v(31.06, -6.6) * mm, "mid": v(31.64, -6.44) * mm, "end": v(32.2, -6.23) * mm});
            skLineSegment(sketch, "E7.43.5", {"start": v(31.06, -6.6) * mm, "end": v(30.01, -6.38) * mm});
            skLineSegment(sketch, "E7.44.0", {"start": v(31.7, -1.66) * mm, "end": v(30.64, -1.6) * mm});
            skArc(sketch, "E7.44.1", {"start": v(31.7, -1.66) * mm, "mid": v(32.23, -1.97) * mm, "end": v(32.72, -2.32) * mm});
            skLineSegment(sketch, "E7.44.2", {"start": v(32.72, -2.32) * mm, "end": v(32.7, -2.57) * mm});
            skLineSegment(sketch, "E7.44.3", {"start": v(32.68, -2.83) * mm, "end": v(32.7, -2.57) * mm});
            skArc(sketch, "E7.44.4", {"start": v(31.58, -3.32) * mm, "mid": v(32.14, -3.1) * mm, "end": v(32.68, -2.83) * mm});
            skLineSegment(sketch, "E7.44.5", {"start": v(31.58, -3.32) * mm, "end": v(30.52, -3.2) * mm});
            skLineSegment(sketch, "E7.45.0", {"start": v(31.7, 1.66) * mm, "end": v(30.64, 1.6) * mm});
            skArc(sketch, "E7.45.1", {"start": v(31.7, 1.66) * mm, "mid": v(32.26, 1.4) * mm, "end": v(32.79, 1.12) * mm});
            skLineSegment(sketch, "E7.45.2", {"start": v(32.79, 1.12) * mm, "end": v(32.8, 0.86) * mm});
            skLineSegment(sketch, "E7.45.3", {"start": v(32.8, 0.6) * mm, "end": v(32.8, 0.86) * mm});
            skArc(sketch, "E7.45.4", {"start": v(31.75, 0) * mm, "mid": v(32.29, 0.28) * mm, "end": v(32.8, 0.6) * mm});
            skLineSegment(sketch, "E7.45.5", {"start": v(31.75, 0) * mm, "end": v(30.68, 0) * mm});
            skLineSegment(sketch, "E7.46.0", {"start": v(31.36, 4.97) * mm, "end": v(30.3, 4.8) * mm});
            skArc(sketch, "E7.46.1", {"start": v(31.36, 4.97) * mm, "mid": v(31.93, 4.77) * mm, "end": v(32.49, 4.54) * mm});
            skLineSegment(sketch, "E7.46.2", {"start": v(32.49, 4.54) * mm, "end": v(32.52, 4.28) * mm});
            skLineSegment(sketch, "E7.46.3", {"start": v(32.56, 4.03) * mm, "end": v(32.52, 4.28) * mm});
            skArc(sketch, "E7.46.4", {"start": v(31.58, 3.32) * mm, "mid": v(32.08, 3.65) * mm, "end": v(32.56, 4.03) * mm});
            skLineSegment(sketch, "E7.46.5", {"start": v(31.58, 3.32) * mm, "end": v(30.52, 3.2) * mm});
            skLineSegment(sketch, "E7.47.0", {"start": v(30.67, 8.22) * mm, "end": v(29.64, 7.94) * mm});
            skArc(sketch, "E7.47.1", {"start": v(30.67, 8.22) * mm, "mid": v(31.26, 8.08) * mm, "end": v(31.84, 7.9) * mm});
            skLineSegment(sketch, "E7.47.2", {"start": v(31.84, 7.9) * mm, "end": v(31.9, 7.66) * mm});
            skLineSegment(sketch, "E7.47.3", {"start": v(31.96, 7.4) * mm, "end": v(31.9, 7.66) * mm});
            skArc(sketch, "E7.47.4", {"start": v(31.06, 6.6) * mm, "mid": v(31.52, 6.99) * mm, "end": v(31.96, 7.4) * mm});
            skLineSegment(sketch, "E7.47.5", {"start": v(31.06, 6.6) * mm, "end": v(30.01, 6.38) * mm});
            skLineSegment(sketch, "E7.48.0", {"start": v(29.64, 11.38) * mm, "end": v(28.65, 11) * mm});
            skArc(sketch, "E7.48.1", {"start": v(29.64, 11.38) * mm, "mid": v(30.24, 11.3) * mm, "end": v(30.84, 11.2) * mm});
            skLineSegment(sketch, "E7.48.2", {"start": v(30.84, 11.2) * mm, "end": v(30.92, 10.95) * mm});
            skLineSegment(sketch, "E7.48.3", {"start": v(31, 10.7) * mm, "end": v(30.92, 10.95) * mm});
            skArc(sketch, "E7.48.4", {"start": v(30.2, 9.81) * mm, "mid": v(30.62, 10.24) * mm, "end": v(31, 10.7) * mm});
            skLineSegment(sketch, "E7.48.5", {"start": v(30.2, 9.81) * mm, "end": v(29.18, 9.48) * mm});
            skLineSegment(sketch, "E7.49.0", {"start": v(28.29, 14.41) * mm, "end": v(27.34, 13.93) * mm});
            skArc(sketch, "E7.49.1", {"start": v(28.29, 14.41) * mm, "mid": v(28.9, 14.4) * mm, "end": v(29.5, 14.35) * mm});
            skLineSegment(sketch, "E7.49.2", {"start": v(29.5, 14.35) * mm, "end": v(29.6, 14.12) * mm});
            skLineSegment(sketch, "E7.49.3", {"start": v(29.72, 13.9) * mm, "end": v(29.6, 14.12) * mm});
            skArc(sketch, "E7.49.4", {"start": v(29, 12.91) * mm, "mid": v(29.38, 13.39) * mm, "end": v(29.72, 13.9) * mm});
            skLineSegment(sketch, "E7.49.5", {"start": v(29, 12.91) * mm, "end": v(28.03, 12.48) * mm});
            skLineSegment(sketch, "E7.50.0", {"start": v(26.63, 17.3) * mm, "end": v(25.73, 16.71) * mm});
            skArc(sketch, "E7.50.1", {"start": v(26.63, 17.3) * mm, "mid": v(27.23, 17.35) * mm, "end": v(27.84, 17.36) * mm});
            skLineSegment(sketch, "E7.50.2", {"start": v(27.84, 17.36) * mm, "end": v(27.97, 17.14) * mm});
            skLineSegment(sketch, "E7.50.3", {"start": v(28.1, 16.92) * mm, "end": v(27.97, 17.14) * mm});
            skArc(sketch, "E7.50.4", {"start": v(27.5, 15.88) * mm, "mid": v(27.82, 16.39) * mm, "end": v(28.1, 16.92) * mm});
            skLineSegment(sketch, "E7.50.5", {"start": v(27.5, 15.88) * mm, "end": v(26.57, 15.34) * mm});
            skLineSegment(sketch, "E7.51.0", {"start": v(24.67, 19.98) * mm, "end": v(23.85, 19.3) * mm});
            skArc(sketch, "E7.51.1", {"start": v(24.67, 19.98) * mm, "mid": v(25.27, 20.1) * mm, "end": v(25.87, 20.17) * mm});
            skLineSegment(sketch, "E7.51.2", {"start": v(25.87, 20.17) * mm, "end": v(26.03, 19.97) * mm});
            skLineSegment(sketch, "E7.51.3", {"start": v(26.18, 19.77) * mm, "end": v(26.03, 19.97) * mm});
            skArc(sketch, "E7.51.4", {"start": v(25.69, 18.66) * mm, "mid": v(25.95, 19.2) * mm, "end": v(26.18, 19.77) * mm});
            skLineSegment(sketch, "E7.51.5", {"start": v(25.69, 18.66) * mm, "end": v(24.82, 18.04) * mm});
            skLineSegment(sketch, "E7.52.0", {"start": v(22.45, 22.45) * mm, "end": v(21.7, 21.7) * mm});
            skArc(sketch, "E7.52.1", {"start": v(22.45, 22.45) * mm, "mid": v(23.03, 22.63) * mm, "end": v(23.62, 22.77) * mm});
            skLineSegment(sketch, "E7.52.2", {"start": v(23.62, 22.77) * mm, "end": v(23.8, 22.58) * mm});
            skLineSegment(sketch, "E7.52.3", {"start": v(23.97, 22.4) * mm, "end": v(23.8, 22.58) * mm});
            skArc(sketch, "E7.52.4", {"start": v(23.6, 21.24) * mm, "mid": v(23.8, 21.81) * mm, "end": v(23.97, 22.4) * mm});
            skLineSegment(sketch, "E7.52.5", {"start": v(23.6, 21.24) * mm, "end": v(22.8, 20.53) * mm});
            skLineSegment(sketch, "E7.53.0", {"start": v(19.98, 24.67) * mm, "end": v(19.3, 23.85) * mm});
            skArc(sketch, "E7.53.1", {"start": v(19.98, 24.67) * mm, "mid": v(20.54, 24.91) * mm, "end": v(21.1, 25.11) * mm});
            skLineSegment(sketch, "E7.53.2", {"start": v(21.1, 25.11) * mm, "end": v(21.3, 24.95) * mm});
            skLineSegment(sketch, "E7.53.3", {"start": v(21.5, 24.78) * mm, "end": v(21.3, 24.95) * mm});
            skArc(sketch, "E7.53.4", {"start": v(21.24, 23.6) * mm, "mid": v(21.4, 24.18) * mm, "end": v(21.5, 24.78) * mm});
            skLineSegment(sketch, "E7.53.5", {"start": v(21.24, 23.6) * mm, "end": v(20.53, 22.8) * mm});
            skLineSegment(sketch, "E7.54.0", {"start": v(17.3, 26.63) * mm, "end": v(16.71, 25.73) * mm});
            skArc(sketch, "E7.54.1", {"start": v(17.3, 26.63) * mm, "mid": v(17.82, 26.92) * mm, "end": v(18.37, 27.18) * mm});
            skLineSegment(sketch, "E7.54.2", {"start": v(18.37, 27.18) * mm, "end": v(18.58, 27.04) * mm});
            skLineSegment(sketch, "E7.54.3", {"start": v(18.8, 26.89) * mm, "end": v(18.58, 27.04) * mm});
            skArc(sketch, "E7.54.4", {"start": v(18.66, 25.69) * mm, "mid": v(18.75, 26.28) * mm, "end": v(18.8, 26.89) * mm});
            skLineSegment(sketch, "E7.54.5", {"start": v(18.66, 25.69) * mm, "end": v(18.04, 24.82) * mm});
            skLineSegment(sketch, "E7.55.0", {"start": v(14.41, 28.29) * mm, "end": v(13.93, 27.34) * mm});
            skArc(sketch, "E7.55.1", {"start": v(14.41, 28.29) * mm, "mid": v(14.9, 28.64) * mm, "end": v(15.43, 28.95) * mm});
            skLineSegment(sketch, "E7.55.2", {"start": v(15.43, 28.95) * mm, "end": v(15.65, 28.83) * mm});
            skLineSegment(sketch, "E7.55.3", {"start": v(15.88, 28.7) * mm, "end": v(15.65, 28.83) * mm});
            skArc(sketch, "E7.55.4", {"start": v(15.87, 27.5) * mm, "mid": v(15.9, 28.1) * mm, "end": v(15.88, 28.7) * mm});
            skLineSegment(sketch, "E7.55.5", {"start": v(15.87, 27.5) * mm, "end": v(15.34, 26.57) * mm});
            skLineSegment(sketch, "E7.56.0", {"start": v(11.38, 29.64) * mm, "end": v(11, 28.65) * mm});
            skArc(sketch, "E7.56.1", {"start": v(11.38, 29.64) * mm, "mid": v(11.83, 30.04) * mm, "end": v(12.32, 30.4) * mm});
            skLineSegment(sketch, "E7.56.2", {"start": v(12.32, 30.4) * mm, "end": v(12.55, 30.3) * mm});
            skLineSegment(sketch, "E7.56.3", {"start": v(12.8, 30.2) * mm, "end": v(12.55, 30.3) * mm});
            skArc(sketch, "E7.56.4", {"start": v(12.91, 29) * mm, "mid": v(12.88, 29.6) * mm, "end": v(12.8, 30.2) * mm});
            skLineSegment(sketch, "E7.56.5", {"start": v(12.91, 29) * mm, "end": v(12.48, 28.03) * mm});
            skLineSegment(sketch, "E7.57.0", {"start": v(8.22, 30.67) * mm, "end": v(7.94, 29.64) * mm});
            skArc(sketch, "E7.57.1", {"start": v(8.22, 30.67) * mm, "mid": v(8.63, 31.11) * mm, "end": v(9.07, 31.53) * mm});
            skLineSegment(sketch, "E7.57.2", {"start": v(9.07, 31.53) * mm, "end": v(9.32, 31.45) * mm});
            skLineSegment(sketch, "E7.57.3", {"start": v(9.56, 31.38) * mm, "end": v(9.32, 31.45) * mm});
            skArc(sketch, "E7.57.4", {"start": v(9.81, 30.2) * mm, "mid": v(9.7, 30.8) * mm, "end": v(9.56, 31.38) * mm});
            skLineSegment(sketch, "E7.57.5", {"start": v(9.81, 30.2) * mm, "end": v(9.48, 29.18) * mm});
            skLineSegment(sketch, "E7.58.0", {"start": v(4.97, 31.36) * mm, "end": v(4.8, 30.3) * mm});
            skArc(sketch, "E7.58.1", {"start": v(4.97, 31.36) * mm, "mid": v(5.33, 31.84) * mm, "end": v(5.73, 32.3) * mm});
            skLineSegment(sketch, "E7.58.2", {"start": v(5.73, 32.3) * mm, "end": v(5.98, 32.26) * mm});
            skLineSegment(sketch, "E7.58.3", {"start": v(6.23, 32.2) * mm, "end": v(5.98, 32.26) * mm});
            skArc(sketch, "E7.58.4", {"start": v(6.6, 31.06) * mm, "mid": v(6.44, 31.64) * mm, "end": v(6.23, 32.2) * mm});
            skLineSegment(sketch, "E7.58.5", {"start": v(6.6, 31.06) * mm, "end": v(6.38, 30.01) * mm});
            skLineSegment(sketch, "E7.59.0", {"start": v(1.66, 31.7) * mm, "end": v(1.6, 30.64) * mm});
            skArc(sketch, "E7.59.1", {"start": v(1.66, 31.7) * mm, "mid": v(1.97, 32.23) * mm, "end": v(2.32, 32.72) * mm});
            skLineSegment(sketch, "E7.59.2", {"start": v(2.32, 32.72) * mm, "end": v(2.57, 32.7) * mm});
            skLineSegment(sketch, "E7.59.3", {"start": v(2.83, 32.68) * mm, "end": v(2.57, 32.7) * mm});
            skArc(sketch, "E7.59.4", {"start": v(3.32, 31.58) * mm, "mid": v(3.1, 32.14) * mm, "end": v(2.83, 32.68) * mm});
            skLineSegment(sketch, "E7.59.5", {"start": v(3.32, 31.58) * mm, "end": v(3.2, 30.52) * mm});
            skArc(sketch, "E8.trimOffspring", {"start": v(-11, 28.65) * mm, "mid": v(-11.74, 28.35) * mm, "end": v(-12.48, 28.03) * mm});
            skArc(sketch, "E9.trimOffspring", {"start": v(-13.93, 27.34) * mm, "mid": v(-14.64, 26.96) * mm, "end": v(-15.34, 26.57) * mm});
            skArc(sketch, "E10.trimOffspring", {"start": v(-16.71, 25.73) * mm, "mid": v(-17.38, 25.29) * mm, "end": v(-18.04, 24.82) * mm});
            skArc(sketch, "E11.trimOffspring", {"start": v(-19.3, 23.85) * mm, "mid": v(-19.93, 23.33) * mm, "end": v(-20.53, 22.8) * mm});
            skArc(sketch, "E12.trimOffspring", {"start": v(-21.7, 21.7) * mm, "mid": v(-22.26, 21.12) * mm, "end": v(-22.8, 20.53) * mm});
            skArc(sketch, "E13.trimOffspring", {"start": v(-23.85, 19.3) * mm, "mid": v(-24.34, 18.68) * mm, "end": v(-24.82, 18.04) * mm});
            skArc(sketch, "E14.trimOffspring", {"start": v(-25.73, 16.71) * mm, "mid": v(-26.16, 16.03) * mm, "end": v(-26.57, 15.34) * mm});
            skArc(sketch, "E15.trimOffspring", {"start": v(-27.34, 13.93) * mm, "mid": v(-27.7, 13.2) * mm, "end": v(-28.03, 12.48) * mm});
            skArc(sketch, "E16.trimOffspring", {"start": v(-28.65, 11) * mm, "mid": v(-28.92, 10.24) * mm, "end": v(-29.18, 9.48) * mm});
            skArc(sketch, "E17.trimOffspring", {"start": v(-29.64, 7.94) * mm, "mid": v(-29.84, 7.16) * mm, "end": v(-30.01, 6.38) * mm});
            skArc(sketch, "E18.trimOffspring", {"start": v(-30.64, 1.6) * mm, "mid": v(-30.67, 0.8) * mm, "end": v(-30.68, 0) * mm});
            skArc(sketch, "E19.trimOffspring", {"start": v(-30.3, 4.8) * mm, "mid": v(-30.42, 4) * mm, "end": v(-30.52, 3.2) * mm});
            skArc(sketch, "E20.trimOffspring", {"start": v(-30.64, -1.6) * mm, "mid": v(-30.59, -2.4) * mm, "end": v(-30.52, -3.2) * mm});
            skArc(sketch, "E21.trimOffspring", {"start": v(-30.3, -4.8) * mm, "mid": v(-30.17, -5.6) * mm, "end": v(-30.01, -6.38) * mm});
            skArc(sketch, "E22.trimOffspring", {"start": v(-29.64, -7.94) * mm, "mid": v(-29.42, -8.71) * mm, "end": v(-29.18, -9.48) * mm});
            skArc(sketch, "E23.trimOffspring", {"start": v(-28.65, -11) * mm, "mid": v(-28.35, -11.74) * mm, "end": v(-28.03, -12.48) * mm});
            skArc(sketch, "E24.trimOffspring", {"start": v(-27.34, -13.93) * mm, "mid": v(-26.96, -14.64) * mm, "end": v(-26.57, -15.34) * mm});
            skArc(sketch, "E25.trimOffspring", {"start": v(-4.8, 30.3) * mm, "mid": v(-5.6, 30.17) * mm, "end": v(-6.38, 30.01) * mm});
            skArc(sketch, "E26.trimOffspring", {"start": v(-1.6, 30.64) * mm, "mid": v(-2.4, 30.59) * mm, "end": v(-3.2, 30.52) * mm});
            skArc(sketch, "E27.trimOffspring", {"start": v(1.6, 30.64) * mm, "mid": v(0.8, 30.67) * mm, "end": v(0, 30.68) * mm});
            skArc(sketch, "E28.trimOffspring", {"start": v(4.8, 30.3) * mm, "mid": v(4, 30.42) * mm, "end": v(3.2, 30.52) * mm});
            skArc(sketch, "E29.trimOffspring", {"start": v(7.94, 29.64) * mm, "mid": v(7.16, 29.84) * mm, "end": v(6.38, 30.01) * mm});
            skArc(sketch, "E30.trimOffspring", {"start": v(11, 28.65) * mm, "mid": v(10.24, 28.92) * mm, "end": v(9.48, 29.18) * mm});
            skArc(sketch, "E31.trimOffspring", {"start": v(13.93, 27.34) * mm, "mid": v(13.2, 27.7) * mm, "end": v(12.48, 28.03) * mm});
            skArc(sketch, "E32.trimOffspring", {"start": v(16.71, 25.73) * mm, "mid": v(16.03, 26.16) * mm, "end": v(15.34, 26.57) * mm});
            skArc(sketch, "E33.trimOffspring", {"start": v(19.3, 23.85) * mm, "mid": v(18.68, 24.34) * mm, "end": v(18.04, 24.82) * mm});
            skArc(sketch, "E34.trimOffspring", {"start": v(21.7, 21.7) * mm, "mid": v(21.12, 22.26) * mm, "end": v(20.53, 22.8) * mm});
            skArc(sketch, "E35.trimOffspring", {"start": v(23.85, 19.3) * mm, "mid": v(23.33, 19.93) * mm, "end": v(22.8, 20.53) * mm});
            skArc(sketch, "E36.trimOffspring", {"start": v(25.73, 16.71) * mm, "mid": v(25.29, 17.38) * mm, "end": v(24.82, 18.04) * mm});
            skArc(sketch, "E37.trimOffspring", {"start": v(27.34, 13.93) * mm, "mid": v(26.96, 14.64) * mm, "end": v(26.57, 15.34) * mm});
            skArc(sketch, "E38.trimOffspring", {"start": v(28.65, 11) * mm, "mid": v(28.35, 11.74) * mm, "end": v(28.03, 12.48) * mm});
            skArc(sketch, "E39.trimOffspring", {"start": v(29.64, 7.94) * mm, "mid": v(29.42, 8.71) * mm, "end": v(29.18, 9.48) * mm});
            skArc(sketch, "E40.trimOffspring", {"start": v(30.3, 4.8) * mm, "mid": v(30.17, 5.6) * mm, "end": v(30.01, 6.38) * mm});
            skArc(sketch, "E41.trimOffspring", {"start": v(30.64, 1.6) * mm, "mid": v(30.59, 2.4) * mm, "end": v(30.52, 3.2) * mm});
            skArc(sketch, "E42.trimOffspring", {"start": v(30.64, -1.6) * mm, "mid": v(30.67, -0.8) * mm, "end": v(30.68, 0) * mm});
            skArc(sketch, "E43.trimOffspring", {"start": v(30.3, -4.8) * mm, "mid": v(30.42, -4) * mm, "end": v(30.52, -3.2) * mm});
            skArc(sketch, "E44.trimOffspring", {"start": v(29.64, -7.94) * mm, "mid": v(29.84, -7.16) * mm, "end": v(30.01, -6.38) * mm});
            skArc(sketch, "E45.trimOffspring", {"start": v(28.65, -11) * mm, "mid": v(28.92, -10.24) * mm, "end": v(29.18, -9.48) * mm});
            skArc(sketch, "E46.trimOffspring", {"start": v(27.34, -13.93) * mm, "mid": v(27.7, -13.2) * mm, "end": v(28.03, -12.48) * mm});
            skArc(sketch, "E47.trimOffspring", {"start": v(25.73, -16.71) * mm, "mid": v(26.16, -16.03) * mm, "end": v(26.57, -15.34) * mm});
            skArc(sketch, "E48.trimOffspring", {"start": v(23.85, -19.3) * mm, "mid": v(24.34, -18.68) * mm, "end": v(24.82, -18.04) * mm});
            skArc(sketch, "E49.trimOffspring", {"start": v(21.7, -21.7) * mm, "mid": v(22.26, -21.12) * mm, "end": v(22.8, -20.53) * mm});
            skArc(sketch, "E50.trimOffspring", {"start": v(19.3, -23.85) * mm, "mid": v(19.93, -23.33) * mm, "end": v(20.53, -22.8) * mm});
            skArc(sketch, "E51.trimOffspring", {"start": v(16.71, -25.73) * mm, "mid": v(17.38, -25.29) * mm, "end": v(18.04, -24.82) * mm});
            skArc(sketch, "E52.trimOffspring", {"start": v(13.93, -27.34) * mm, "mid": v(14.64, -26.96) * mm, "end": v(15.34, -26.57) * mm});
            skArc(sketch, "E53.trimOffspring", {"start": v(11, -28.65) * mm, "mid": v(11.74, -28.35) * mm, "end": v(12.48, -28.03) * mm});
            skArc(sketch, "E54.trimOffspring", {"start": v(7.94, -29.64) * mm, "mid": v(8.71, -29.42) * mm, "end": v(9.48, -29.18) * mm});
            skArc(sketch, "E55.trimOffspring", {"start": v(4.8, -30.3) * mm, "mid": v(5.6, -30.17) * mm, "end": v(6.38, -30.01) * mm});
            skArc(sketch, "E56.trimOffspring", {"start": v(1.6, -30.64) * mm, "mid": v(2.4, -30.59) * mm, "end": v(3.2, -30.52) * mm});
            skArc(sketch, "E57.trimOffspring", {"start": v(-1.6, -30.64) * mm, "mid": v(-0.8, -30.67) * mm, "end": v(0, -30.68) * mm});
            skArc(sketch, "E58.trimOffspring", {"start": v(-4.8, -30.3) * mm, "mid": v(-4, -30.42) * mm, "end": v(-3.2, -30.52) * mm});
            skArc(sketch, "E59.trimOffspring", {"start": v(-7.94, -29.64) * mm, "mid": v(-7.16, -29.84) * mm, "end": v(-6.38, -30.01) * mm});
            skArc(sketch, "E60.trimOffspring", {"start": v(-11, -28.65) * mm, "mid": v(-10.24, -28.92) * mm, "end": v(-9.48, -29.18) * mm});
            skArc(sketch, "E61.trimOffspring", {"start": v(-13.93, -27.34) * mm, "mid": v(-13.2, -27.7) * mm, "end": v(-12.48, -28.03) * mm});
            skArc(sketch, "E62.trimOffspring", {"start": v(-16.71, -25.73) * mm, "mid": v(-16.03, -26.16) * mm, "end": v(-15.34, -26.57) * mm});
            skArc(sketch, "E63.trimOffspring", {"start": v(-19.3, -23.85) * mm, "mid": v(-18.68, -24.34) * mm, "end": v(-18.04, -24.82) * mm});
            skArc(sketch, "E64.trimOffspring", {"start": v(-21.7, -21.7) * mm, "mid": v(-21.12, -22.26) * mm, "end": v(-20.53, -22.8) * mm});
            skArc(sketch, "E65.trimOffspring", {"start": v(-23.85, -19.3) * mm, "mid": v(-23.33, -19.93) * mm, "end": v(-22.8, -20.53) * mm});
            skArc(sketch, "E66.trimOffspring", {"start": v(-25.73, -16.71) * mm, "mid": v(-25.29, -17.38) * mm, "end": v(-24.82, -18.04) * mm});
            skSolve(sketch);
        }
        {
            var Q0;
            Q0 = qSketchRegion(id + "F0", true);
            var Q1;
            Q1=makeQuery(id+"F0.imprint","IMPRINT",FACE,{"disambiguationData":[TD([[makeQuery(id+"F0.imprint","IMPRINT",EDGE,{"derivedFrom":sQuery(id+"F0.wireOp",EDGE,"E0")}),1.0]])]});
            extrude(context, id + "F1", {"entities" : qUnion([Q0, Q1]), "depth" : 25.4 * mm});
        }
        {
            var Q0;
            Q0=makeQuery(id+"F1.opExtrude","CAP_FACE",FACE,{"disambiguationData":[OSD([sQuery(id+"F0.wireOp",EDGE,"E0"),sQuery(id+"F0.wireOp",EDGE,"E1.trimOffspring"),sQuery(id+"F0.wireOp",EDGE,"E2"),sQuery(id+"F0.wireOp",EDGE,"E3"),sQuery(id+"F0.wireOp",EDGE,"E4.MirrorCS"),sQuery(id+"F0.wireOp",EDGE,"E5.MirrorCS"),sQuery(id+"F0.wireOp",EDGE,"E6.MirrorCS"),sQuery(id+"F0.wireOp",EDGE,"E7.1.0"),sQuery(id+"F0.wireOp",EDGE,"E7.1.1"),sQuery(id+"F0.wireOp",EDGE,"E7.1.2"),sQuery(id+"F0.wireOp",EDGE,"E7.1.3"),sQuery(id+"F0.wireOp",EDGE,"E7.1.4"),sQuery(id+"F0.wireOp",EDGE,"E7.1.5"),sQuery(id+"F0.wireOp",EDGE,"E7.2.0"),sQuery(id+"F0.wireOp",EDGE,"E7.2.1"),sQuery(id+"F0.wireOp",EDGE,"E7.2.2"),sQuery(id+"F0.wireOp",EDGE,"E7.2.3"),sQuery(id+"F0.wireOp",EDGE,"E7.2.4"),sQuery(id+"F0.wireOp",EDGE,"E7.2.5"),sQuery(id+"F0.wireOp",EDGE,"E7.3.0"),sQuery(id+"F0.wireOp",EDGE,"E7.3.1"),sQuery(id+"F0.wireOp",EDGE,"E7.3.2"),sQuery(id+"F0.wireOp",EDGE,"E7.3.3"),sQuery(id+"F0.wireOp",EDGE,"E7.3.4"),sQuery(id+"F0.wireOp",EDGE,"E7.3.5"),sQuery(id+"F0.wireOp",EDGE,"E7.4.0"),sQuery(id+"F0.wireOp",EDGE,"E7.4.1"),sQuery(id+"F0.wireOp",EDGE,"E7.4.2"),sQuery(id+"F0.wireOp",EDGE,"E7.4.3"),sQuery(id+"F0.wireOp",EDGE,"E7.4.4"),sQuery(id+"F0.wireOp",EDGE,"E7.4.5"),sQuery(id+"F0.wireOp",EDGE,"E7.5.0"),sQuery(id+"F0.wireOp",EDGE,"E7.5.1"),sQuery(id+"F0.wireOp",EDGE,"E7.5.2"),sQuery(id+"F0.wireOp",EDGE,"E7.5.3"),sQuery(id+"F0.wireOp",EDGE,"E7.5.4"),sQuery(id+"F0.wireOp",EDGE,"E7.5.5"),sQuery(id+"F0.wireOp",EDGE,"E7.6.0"),sQuery(id+"F0.wireOp",EDGE,"E7.6.1"),sQuery(id+"F0.wireOp",EDGE,"E7.6.2"),sQuery(id+"F0.wireOp",EDGE,"E7.6.3"),sQuery(id+"F0.wireOp",EDGE,"E7.6.4"),sQuery(id+"F0.wireOp",EDGE,"E7.6.5"),sQuery(id+"F0.wireOp",EDGE,"E7.7.0"),sQuery(id+"F0.wireOp",EDGE,"E7.7.1"),sQuery(id+"F0.wireOp",EDGE,"E7.7.2"),sQuery(id+"F0.wireOp",EDGE,"E7.7.3"),sQuery(id+"F0.wireOp",EDGE,"E7.7.4"),sQuery(id+"F0.wireOp",EDGE,"E7.7.5"),sQuery(id+"F0.wireOp",EDGE,"E7.8.0"),sQuery(id+"F0.wireOp",EDGE,"E7.8.1"),sQuery(id+"F0.wireOp",EDGE,"E7.8.2"),sQuery(id+"F0.wireOp",EDGE,"E7.8.3"),sQuery(id+"F0.wireOp",EDGE,"E7.8.4"),sQuery(id+"F0.wireOp",EDGE,"E7.8.5"),sQuery(id+"F0.wireOp",EDGE,"E7.9.0"),sQuery(id+"F0.wireOp",EDGE,"E7.9.1"),sQuery(id+"F0.wireOp",EDGE,"E7.9.2"),sQuery(id+"F0.wireOp",EDGE,"E7.9.3"),sQuery(id+"F0.wireOp",EDGE,"E7.9.4"),sQuery(id+"F0.wireOp",EDGE,"E7.9.5"),sQuery(id+"F0.wireOp",EDGE,"E7.10.0"),sQuery(id+"F0.wireOp",EDGE,"E7.10.1"),sQuery(id+"F0.wireOp",EDGE,"E7.10.2"),sQuery(id+"F0.wireOp",EDGE,"E7.10.3"),sQuery(id+"F0.wireOp",EDGE,"E7.10.4"),sQuery(id+"F0.wireOp",EDGE,"E7.10.5"),sQuery(id+"F0.wireOp",EDGE,"E7.11.0"),sQuery(id+"F0.wireOp",EDGE,"E7.11.1"),sQuery(id+"F0.wireOp",EDGE,"E7.11.2"),sQuery(id+"F0.wireOp",EDGE,"E7.11.3"),sQuery(id+"F0.wireOp",EDGE,"E7.11.4"),sQuery(id+"F0.wireOp",EDGE,"E7.11.5"),sQuery(id+"F0.wireOp",EDGE,"E7.12.0"),sQuery(id+"F0.wireOp",EDGE,"E7.12.1"),sQuery(id+"F0.wireOp",EDGE,"E7.12.2"),sQuery(id+"F0.wireOp",EDGE,"E7.12.3"),sQuery(id+"F0.wireOp",EDGE,"E7.12.4"),sQuery(id+"F0.wireOp",EDGE,"E7.12.5"),sQuery(id+"F0.wireOp",EDGE,"E7.13.0"),sQuery(id+"F0.wireOp",EDGE,"E7.13.1"),sQuery(id+"F0.wireOp",EDGE,"E7.13.2"),sQuery(id+"F0.wireOp",EDGE,"E7.13.3"),sQuery(id+"F0.wireOp",EDGE,"E7.13.4"),sQuery(id+"F0.wireOp",EDGE,"E7.13.5"),sQuery(id+"F0.wireOp",EDGE,"E7.14.0"),sQuery(id+"F0.wireOp",EDGE,"E7.14.1"),sQuery(id+"F0.wireOp",EDGE,"E7.14.2"),sQuery(id+"F0.wireOp",EDGE,"E7.14.3"),sQuery(id+"F0.wireOp",EDGE,"E7.14.4"),sQuery(id+"F0.wireOp",EDGE,"E7.14.5"),sQuery(id+"F0.wireOp",EDGE,"E7.15.0"),sQuery(id+"F0.wireOp",EDGE,"E7.15.1"),sQuery(id+"F0.wireOp",EDGE,"E7.15.2"),sQuery(id+"F0.wireOp",EDGE,"E7.15.3"),sQuery(id+"F0.wireOp",EDGE,"E7.15.4"),sQuery(id+"F0.wireOp",EDGE,"E7.15.5"),sQuery(id+"F0.wireOp",EDGE,"E7.16.0"),sQuery(id+"F0.wireOp",EDGE,"E7.16.1"),sQuery(id+"F0.wireOp",EDGE,"E7.16.2"),sQuery(id+"F0.wireOp",EDGE,"E7.16.3"),sQuery(id+"F0.wireOp",EDGE,"E7.16.4"),sQuery(id+"F0.wireOp",EDGE,"E7.16.5"),sQuery(id+"F0.wireOp",EDGE,"E7.17.0"),sQuery(id+"F0.wireOp",EDGE,"E7.17.1"),sQuery(id+"F0.wireOp",EDGE,"E7.17.2"),sQuery(id+"F0.wireOp",EDGE,"E7.17.3"),sQuery(id+"F0.wireOp",EDGE,"E7.17.4"),sQuery(id+"F0.wireOp",EDGE,"E7.17.5"),sQuery(id+"F0.wireOp",EDGE,"E7.18.0"),sQuery(id+"F0.wireOp",EDGE,"E7.18.1"),sQuery(id+"F0.wireOp",EDGE,"E7.18.2"),sQuery(id+"F0.wireOp",EDGE,"E7.18.3"),sQuery(id+"F0.wireOp",EDGE,"E7.18.4"),sQuery(id+"F0.wireOp",EDGE,"E7.18.5"),sQuery(id+"F0.wireOp",EDGE,"E7.19.0"),sQuery(id+"F0.wireOp",EDGE,"E7.19.1"),sQuery(id+"F0.wireOp",EDGE,"E7.19.2"),sQuery(id+"F0.wireOp",EDGE,"E7.19.3"),sQuery(id+"F0.wireOp",EDGE,"E7.19.4"),sQuery(id+"F0.wireOp",EDGE,"E7.19.5"),sQuery(id+"F0.wireOp",EDGE,"E7.20.0"),sQuery(id+"F0.wireOp",EDGE,"E7.20.1"),sQuery(id+"F0.wireOp",EDGE,"E7.20.2"),sQuery(id+"F0.wireOp",EDGE,"E7.20.3"),sQuery(id+"F0.wireOp",EDGE,"E7.20.4"),sQuery(id+"F0.wireOp",EDGE,"E7.20.5"),sQuery(id+"F0.wireOp",EDGE,"E7.21.0"),sQuery(id+"F0.wireOp",EDGE,"E7.21.1"),sQuery(id+"F0.wireOp",EDGE,"E7.21.2"),sQuery(id+"F0.wireOp",EDGE,"E7.21.3"),sQuery(id+"F0.wireOp",EDGE,"E7.21.4"),sQuery(id+"F0.wireOp",EDGE,"E7.21.5"),sQuery(id+"F0.wireOp",EDGE,"E7.22.0"),sQuery(id+"F0.wireOp",EDGE,"E7.22.1"),sQuery(id+"F0.wireOp",EDGE,"E7.22.2"),sQuery(id+"F0.wireOp",EDGE,"E7.22.3"),sQuery(id+"F0.wireOp",EDGE,"E7.22.4"),sQuery(id+"F0.wireOp",EDGE,"E7.22.5"),sQuery(id+"F0.wireOp",EDGE,"E7.23.0"),sQuery(id+"F0.wireOp",EDGE,"E7.23.1"),sQuery(id+"F0.wireOp",EDGE,"E7.23.2"),sQuery(id+"F0.wireOp",EDGE,"E7.23.3"),sQuery(id+"F0.wireOp",EDGE,"E7.23.4"),sQuery(id+"F0.wireOp",EDGE,"E7.23.5"),sQuery(id+"F0.wireOp",EDGE,"E7.24.0"),sQuery(id+"F0.wireOp",EDGE,"E7.24.1"),sQuery(id+"F0.wireOp",EDGE,"E7.24.2"),sQuery(id+"F0.wireOp",EDGE,"E7.24.3"),sQuery(id+"F0.wireOp",EDGE,"E7.24.4"),sQuery(id+"F0.wireOp",EDGE,"E7.24.5"),sQuery(id+"F0.wireOp",EDGE,"E7.25.0"),sQuery(id+"F0.wireOp",EDGE,"E7.25.1"),sQuery(id+"F0.wireOp",EDGE,"E7.25.2"),sQuery(id+"F0.wireOp",EDGE,"E7.25.3"),sQuery(id+"F0.wireOp",EDGE,"E7.25.4"),sQuery(id+"F0.wireOp",EDGE,"E7.25.5"),sQuery(id+"F0.wireOp",EDGE,"E7.26.0"),sQuery(id+"F0.wireOp",EDGE,"E7.26.1"),sQuery(id+"F0.wireOp",EDGE,"E7.26.2"),sQuery(id+"F0.wireOp",EDGE,"E7.26.3"),sQuery(id+"F0.wireOp",EDGE,"E7.26.4"),sQuery(id+"F0.wireOp",EDGE,"E7.26.5"),sQuery(id+"F0.wireOp",EDGE,"E7.27.0"),sQuery(id+"F0.wireOp",EDGE,"E7.27.1"),sQuery(id+"F0.wireOp",EDGE,"E7.27.2"),sQuery(id+"F0.wireOp",EDGE,"E7.27.3"),sQuery(id+"F0.wireOp",EDGE,"E7.27.4"),sQuery(id+"F0.wireOp",EDGE,"E7.27.5"),sQuery(id+"F0.wireOp",EDGE,"E7.28.0"),sQuery(id+"F0.wireOp",EDGE,"E7.28.1"),sQuery(id+"F0.wireOp",EDGE,"E7.28.2"),sQuery(id+"F0.wireOp",EDGE,"E7.28.3"),sQuery(id+"F0.wireOp",EDGE,"E7.28.4"),sQuery(id+"F0.wireOp",EDGE,"E7.28.5"),sQuery(id+"F0.wireOp",EDGE,"E7.29.0"),sQuery(id+"F0.wireOp",EDGE,"E7.29.1"),sQuery(id+"F0.wireOp",EDGE,"E7.29.2"),sQuery(id+"F0.wireOp",EDGE,"E7.29.3"),sQuery(id+"F0.wireOp",EDGE,"E7.29.4"),sQuery(id+"F0.wireOp",EDGE,"E7.29.5"),sQuery(id+"F0.wireOp",EDGE,"E7.30.0"),sQuery(id+"F0.wireOp",EDGE,"E7.30.1"),sQuery(id+"F0.wireOp",EDGE,"E7.30.2"),sQuery(id+"F0.wireOp",EDGE,"E7.30.3"),sQuery(id+"F0.wireOp",EDGE,"E7.30.4"),sQuery(id+"F0.wireOp",EDGE,"E7.30.5"),sQuery(id+"F0.wireOp",EDGE,"E7.31.0"),sQuery(id+"F0.wireOp",EDGE,"E7.31.1"),sQuery(id+"F0.wireOp",EDGE,"E7.31.2"),sQuery(id+"F0.wireOp",EDGE,"E7.31.3"),sQuery(id+"F0.wireOp",EDGE,"E7.31.4"),sQuery(id+"F0.wireOp",EDGE,"E7.31.5"),sQuery(id+"F0.wireOp",EDGE,"E7.32.0"),sQuery(id+"F0.wireOp",EDGE,"E7.32.1"),sQuery(id+"F0.wireOp",EDGE,"E7.32.2"),sQuery(id+"F0.wireOp",EDGE,"E7.32.3"),sQuery(id+"F0.wireOp",EDGE,"E7.32.4"),sQuery(id+"F0.wireOp",EDGE,"E7.32.5"),sQuery(id+"F0.wireOp",EDGE,"E7.33.0"),sQuery(id+"F0.wireOp",EDGE,"E7.33.1"),sQuery(id+"F0.wireOp",EDGE,"E7.33.2"),sQuery(id+"F0.wireOp",EDGE,"E7.33.3"),sQuery(id+"F0.wireOp",EDGE,"E7.33.4"),sQuery(id+"F0.wireOp",EDGE,"E7.33.5"),sQuery(id+"F0.wireOp",EDGE,"E7.34.0"),sQuery(id+"F0.wireOp",EDGE,"E7.34.1"),sQuery(id+"F0.wireOp",EDGE,"E7.34.2"),sQuery(id+"F0.wireOp",EDGE,"E7.34.3"),sQuery(id+"F0.wireOp",EDGE,"E7.34.4"),sQuery(id+"F0.wireOp",EDGE,"E7.34.5"),sQuery(id+"F0.wireOp",EDGE,"E7.35.0"),sQuery(id+"F0.wireOp",EDGE,"E7.35.1"),sQuery(id+"F0.wireOp",EDGE,"E7.35.2"),sQuery(id+"F0.wireOp",EDGE,"E7.35.3"),sQuery(id+"F0.wireOp",EDGE,"E7.35.4"),sQuery(id+"F0.wireOp",EDGE,"E7.35.5"),sQuery(id+"F0.wireOp",EDGE,"E7.36.0"),sQuery(id+"F0.wireOp",EDGE,"E7.36.1"),sQuery(id+"F0.wireOp",EDGE,"E7.36.2"),sQuery(id+"F0.wireOp",EDGE,"E7.36.3"),sQuery(id+"F0.wireOp",EDGE,"E7.36.4"),sQuery(id+"F0.wireOp",EDGE,"E7.36.5"),sQuery(id+"F0.wireOp",EDGE,"E7.37.0"),sQuery(id+"F0.wireOp",EDGE,"E7.37.1"),sQuery(id+"F0.wireOp",EDGE,"E7.37.2"),sQuery(id+"F0.wireOp",EDGE,"E7.37.3"),sQuery(id+"F0.wireOp",EDGE,"E7.37.4"),sQuery(id+"F0.wireOp",EDGE,"E7.37.5"),sQuery(id+"F0.wireOp",EDGE,"E7.38.0"),sQuery(id+"F0.wireOp",EDGE,"E7.38.1"),sQuery(id+"F0.wireOp",EDGE,"E7.38.2"),sQuery(id+"F0.wireOp",EDGE,"E7.38.3"),sQuery(id+"F0.wireOp",EDGE,"E7.38.4"),sQuery(id+"F0.wireOp",EDGE,"E7.38.5"),sQuery(id+"F0.wireOp",EDGE,"E7.39.0"),sQuery(id+"F0.wireOp",EDGE,"E7.39.1"),sQuery(id+"F0.wireOp",EDGE,"E7.39.2"),sQuery(id+"F0.wireOp",EDGE,"E7.39.3"),sQuery(id+"F0.wireOp",EDGE,"E7.39.4"),sQuery(id+"F0.wireOp",EDGE,"E7.39.5"),sQuery(id+"F0.wireOp",EDGE,"E7.40.0"),sQuery(id+"F0.wireOp",EDGE,"E7.40.1"),sQuery(id+"F0.wireOp",EDGE,"E7.40.2"),sQuery(id+"F0.wireOp",EDGE,"E7.40.3"),sQuery(id+"F0.wireOp",EDGE,"E7.40.4"),sQuery(id+"F0.wireOp",EDGE,"E7.40.5"),sQuery(id+"F0.wireOp",EDGE,"E7.41.0"),sQuery(id+"F0.wireOp",EDGE,"E7.41.1"),sQuery(id+"F0.wireOp",EDGE,"E7.41.2"),sQuery(id+"F0.wireOp",EDGE,"E7.41.3"),sQuery(id+"F0.wireOp",EDGE,"E7.41.4"),sQuery(id+"F0.wireOp",EDGE,"E7.41.5"),sQuery(id+"F0.wireOp",EDGE,"E7.42.0"),sQuery(id+"F0.wireOp",EDGE,"E7.42.1"),sQuery(id+"F0.wireOp",EDGE,"E7.42.2"),sQuery(id+"F0.wireOp",EDGE,"E7.42.3"),sQuery(id+"F0.wireOp",EDGE,"E7.42.4"),sQuery(id+"F0.wireOp",EDGE,"E7.42.5"),sQuery(id+"F0.wireOp",EDGE,"E7.43.0"),sQuery(id+"F0.wireOp",EDGE,"E7.43.1"),sQuery(id+"F0.wireOp",EDGE,"E7.43.2"),sQuery(id+"F0.wireOp",EDGE,"E7.43.3"),sQuery(id+"F0.wireOp",EDGE,"E7.43.4"),sQuery(id+"F0.wireOp",EDGE,"E7.43.5"),sQuery(id+"F0.wireOp",EDGE,"E7.44.0"),sQuery(id+"F0.wireOp",EDGE,"E7.44.1"),sQuery(id+"F0.wireOp",EDGE,"E7.44.2"),sQuery(id+"F0.wireOp",EDGE,"E7.44.3"),sQuery(id+"F0.wireOp",EDGE,"E7.44.4"),sQuery(id+"F0.wireOp",EDGE,"E7.44.5"),sQuery(id+"F0.wireOp",EDGE,"E7.45.0"),sQuery(id+"F0.wireOp",EDGE,"E7.45.1"),sQuery(id+"F0.wireOp",EDGE,"E7.45.2"),sQuery(id+"F0.wireOp",EDGE,"E7.45.3"),sQuery(id+"F0.wireOp",EDGE,"E7.45.4"),sQuery(id+"F0.wireOp",EDGE,"E7.45.5"),sQuery(id+"F0.wireOp",EDGE,"E7.46.0"),sQuery(id+"F0.wireOp",EDGE,"E7.46.1"),sQuery(id+"F0.wireOp",EDGE,"E7.46.2"),sQuery(id+"F0.wireOp",EDGE,"E7.46.3"),sQuery(id+"F0.wireOp",EDGE,"E7.46.4"),sQuery(id+"F0.wireOp",EDGE,"E7.46.5"),sQuery(id+"F0.wireOp",EDGE,"E7.47.0"),sQuery(id+"F0.wireOp",EDGE,"E7.47.1"),sQuery(id+"F0.wireOp",EDGE,"E7.47.2"),sQuery(id+"F0.wireOp",EDGE,"E7.47.3"),sQuery(id+"F0.wireOp",EDGE,"E7.47.4"),sQuery(id+"F0.wireOp",EDGE,"E7.47.5"),sQuery(id+"F0.wireOp",EDGE,"E7.48.0"),sQuery(id+"F0.wireOp",EDGE,"E7.48.1"),sQuery(id+"F0.wireOp",EDGE,"E7.48.2"),sQuery(id+"F0.wireOp",EDGE,"E7.48.3"),sQuery(id+"F0.wireOp",EDGE,"E7.48.4"),sQuery(id+"F0.wireOp",EDGE,"E7.48.5"),sQuery(id+"F0.wireOp",EDGE,"E7.49.0"),sQuery(id+"F0.wireOp",EDGE,"E7.49.1"),sQuery(id+"F0.wireOp",EDGE,"E7.49.2"),sQuery(id+"F0.wireOp",EDGE,"E7.49.3"),sQuery(id+"F0.wireOp",EDGE,"E7.49.4"),sQuery(id+"F0.wireOp",EDGE,"E7.49.5"),sQuery(id+"F0.wireOp",EDGE,"E7.50.0"),sQuery(id+"F0.wireOp",EDGE,"E7.50.1"),sQuery(id+"F0.wireOp",EDGE,"E7.50.2"),sQuery(id+"F0.wireOp",EDGE,"E7.50.3"),sQuery(id+"F0.wireOp",EDGE,"E7.50.4"),sQuery(id+"F0.wireOp",EDGE,"E7.50.5"),sQuery(id+"F0.wireOp",EDGE,"E7.51.0"),sQuery(id+"F0.wireOp",EDGE,"E7.51.1"),sQuery(id+"F0.wireOp",EDGE,"E7.51.2"),sQuery(id+"F0.wireOp",EDGE,"E7.51.3"),sQuery(id+"F0.wireOp",EDGE,"E7.51.4"),sQuery(id+"F0.wireOp",EDGE,"E7.51.5"),sQuery(id+"F0.wireOp",EDGE,"E7.52.0"),sQuery(id+"F0.wireOp",EDGE,"E7.52.1"),sQuery(id+"F0.wireOp",EDGE,"E7.52.2"),sQuery(id+"F0.wireOp",EDGE,"E7.52.3"),sQuery(id+"F0.wireOp",EDGE,"E7.52.4"),sQuery(id+"F0.wireOp",EDGE,"E7.52.5"),sQuery(id+"F0.wireOp",EDGE,"E7.53.0"),sQuery(id+"F0.wireOp",EDGE,"E7.53.1"),sQuery(id+"F0.wireOp",EDGE,"E7.53.2"),sQuery(id+"F0.wireOp",EDGE,"E7.53.3"),sQuery(id+"F0.wireOp",EDGE,"E7.53.4"),sQuery(id+"F0.wireOp",EDGE,"E7.53.5"),sQuery(id+"F0.wireOp",EDGE,"E7.54.0"),sQuery(id+"F0.wireOp",EDGE,"E7.54.1"),sQuery(id+"F0.wireOp",EDGE,"E7.54.2"),sQuery(id+"F0.wireOp",EDGE,"E7.54.3"),sQuery(id+"F0.wireOp",EDGE,"E7.54.4"),sQuery(id+"F0.wireOp",EDGE,"E7.54.5"),sQuery(id+"F0.wireOp",EDGE,"E7.55.0"),sQuery(id+"F0.wireOp",EDGE,"E7.55.1"),sQuery(id+"F0.wireOp",EDGE,"E7.55.2"),sQuery(id+"F0.wireOp",EDGE,"E7.55.3"),sQuery(id+"F0.wireOp",EDGE,"E7.55.4"),sQuery(id+"F0.wireOp",EDGE,"E7.55.5"),sQuery(id+"F0.wireOp",EDGE,"E7.56.0"),sQuery(id+"F0.wireOp",EDGE,"E7.56.1"),sQuery(id+"F0.wireOp",EDGE,"E7.56.2"),sQuery(id+"F0.wireOp",EDGE,"E7.56.3"),sQuery(id+"F0.wireOp",EDGE,"E7.56.4"),sQuery(id+"F0.wireOp",EDGE,"E7.56.5"),sQuery(id+"F0.wireOp",EDGE,"E7.57.0"),sQuery(id+"F0.wireOp",EDGE,"E7.57.1"),sQuery(id+"F0.wireOp",EDGE,"E7.57.2"),sQuery(id+"F0.wireOp",EDGE,"E7.57.3"),sQuery(id+"F0.wireOp",EDGE,"E7.57.4"),sQuery(id+"F0.wireOp",EDGE,"E7.57.5"),sQuery(id+"F0.wireOp",EDGE,"E7.58.0"),sQuery(id+"F0.wireOp",EDGE,"E7.58.1"),sQuery(id+"F0.wireOp",EDGE,"E7.58.2"),sQuery(id+"F0.wireOp",EDGE,"E7.58.3"),sQuery(id+"F0.wireOp",EDGE,"E7.58.4"),sQuery(id+"F0.wireOp",EDGE,"E7.58.5"),sQuery(id+"F0.wireOp",EDGE,"E7.59.0"),sQuery(id+"F0.wireOp",EDGE,"E7.59.1"),sQuery(id+"F0.wireOp",EDGE,"E7.59.2"),sQuery(id+"F0.wireOp",EDGE,"E7.59.3"),sQuery(id+"F0.wireOp",EDGE,"E7.59.4"),sQuery(id+"F0.wireOp",EDGE,"E7.59.5"),sQuery(id+"F0.wireOp",EDGE,"E8.trimOffspring"),sQuery(id+"F0.wireOp",EDGE,"E9.trimOffspring"),sQuery(id+"F0.wireOp",EDGE,"E10.trimOffspring"),sQuery(id+"F0.wireOp",EDGE,"E11.trimOffspring"),sQuery(id+"F0.wireOp",EDGE,"E12.trimOffspring"),sQuery(id+"F0.wireOp",EDGE,"E13.trimOffspring"),sQuery(id+"F0.wireOp",EDGE,"E14.trimOffspring"),sQuery(id+"F0.wireOp",EDGE,"E15.trimOffspring"),sQuery(id+"F0.wireOp",EDGE,"E16.trimOffspring"),sQuery(id+"F0.wireOp",EDGE,"E17.trimOffspring"),sQuery(id+"F0.wireOp",EDGE,"E18.trimOffspring"),sQuery(id+"F0.wireOp",EDGE,"E19.trimOffspring"),sQuery(id+"F0.wireOp",EDGE,"E20.trimOffspring"),sQuery(id+"F0.wireOp",EDGE,"E21.trimOffspring"),sQuery(id+"F0.wireOp",EDGE,"E22.trimOffspring"),sQuery(id+"F0.wireOp",EDGE,"E23.trimOffspring"),sQuery(id+"F0.wireOp",EDGE,"E24.trimOffspring"),sQuery(id+"F0.wireOp",EDGE,"E25.trimOffspring"),sQuery(id+"F0.wireOp",EDGE,"E26.trimOffspring"),sQuery(id+"F0.wireOp",EDGE,"E27.trimOffspring"),sQuery(id+"F0.wireOp",EDGE,"E28.trimOffspring"),sQuery(id+"F0.wireOp",EDGE,"E29.trimOffspring"),sQuery(id+"F0.wireOp",EDGE,"E30.trimOffspring"),sQuery(id+"F0.wireOp",EDGE,"E31.trimOffspring"),sQuery(id+"F0.wireOp",EDGE,"E32.trimOffspring"),sQuery(id+"F0.wireOp",EDGE,"E33.trimOffspring"),sQuery(id+"F0.wireOp",EDGE,"E34.trimOffspring"),sQuery(id+"F0.wireOp",EDGE,"E35.trimOffspring"),sQuery(id+"F0.wireOp",EDGE,"E36.trimOffspring"),sQuery(id+"F0.wireOp",EDGE,"E37.trimOffspring"),sQuery(id+"F0.wireOp",EDGE,"E38.trimOffspring"),sQuery(id+"F0.wireOp",EDGE,"E39.trimOffspring"),sQuery(id+"F0.wireOp",EDGE,"E40.trimOffspring"),sQuery(id+"F0.wireOp",EDGE,"E41.trimOffspring"),sQuery(id+"F0.wireOp",EDGE,"E42.trimOffspring"),sQuery(id+"F0.wireOp",EDGE,"E43.trimOffspring"),sQuery(id+"F0.wireOp",EDGE,"E44.trimOffspring"),sQuery(id+"F0.wireOp",EDGE,"E45.trimOffspring"),sQuery(id+"F0.wireOp",EDGE,"E46.trimOffspring"),sQuery(id+"F0.wireOp",EDGE,"E47.trimOffspring"),sQuery(id+"F0.wireOp",EDGE,"E48.trimOffspring"),sQuery(id+"F0.wireOp",EDGE,"E49.trimOffspring"),sQuery(id+"F0.wireOp",EDGE,"E50.trimOffspring"),sQuery(id+"F0.wireOp",EDGE,"E51.trimOffspring"),sQuery(id+"F0.wireOp",EDGE,"E52.trimOffspring"),sQuery(id+"F0.wireOp",EDGE,"E53.trimOffspring"),sQuery(id+"F0.wireOp",EDGE,"E54.trimOffspring"),sQuery(id+"F0.wireOp",EDGE,"E55.trimOffspring"),sQuery(id+"F0.wireOp",EDGE,"E56.trimOffspring"),sQuery(id+"F0.wireOp",EDGE,"E57.trimOffspring"),sQuery(id+"F0.wireOp",EDGE,"E58.trimOffspring"),sQuery(id+"F0.wireOp",EDGE,"E59.trimOffspring"),sQuery(id+"F0.wireOp",EDGE,"E60.trimOffspring"),sQuery(id+"F0.wireOp",EDGE,"E61.trimOffspring"),sQuery(id+"F0.wireOp",EDGE,"E62.trimOffspring"),sQuery(id+"F0.wireOp",EDGE,"E63.trimOffspring"),sQuery(id+"F0.wireOp",EDGE,"E64.trimOffspring"),sQuery(id+"F0.wireOp",EDGE,"E65.trimOffspring"),sQuery(id+"F0.wireOp",EDGE,"E66.trimOffspring")])],"isStart":false});
            var sketch = newSketch(context, id + "F2", { "sketchPlane" : qUnion([Q0])});
            skCircle(sketch, "E67", {"center": v(0, 0) * mm, "radius": 11.43 * mm});
            skSolve(sketch);
        }
        {
            var Q0;
            Q0 = qSketchRegion(id + "F2", true);
            extrude(context, id + "F3", {"entities" : qUnion([Q0]), "operationType" : NewBodyOperationType.REMOVE, "oppositeDirection" : true, "depth" : 25.4 * mm});
        }
    });
